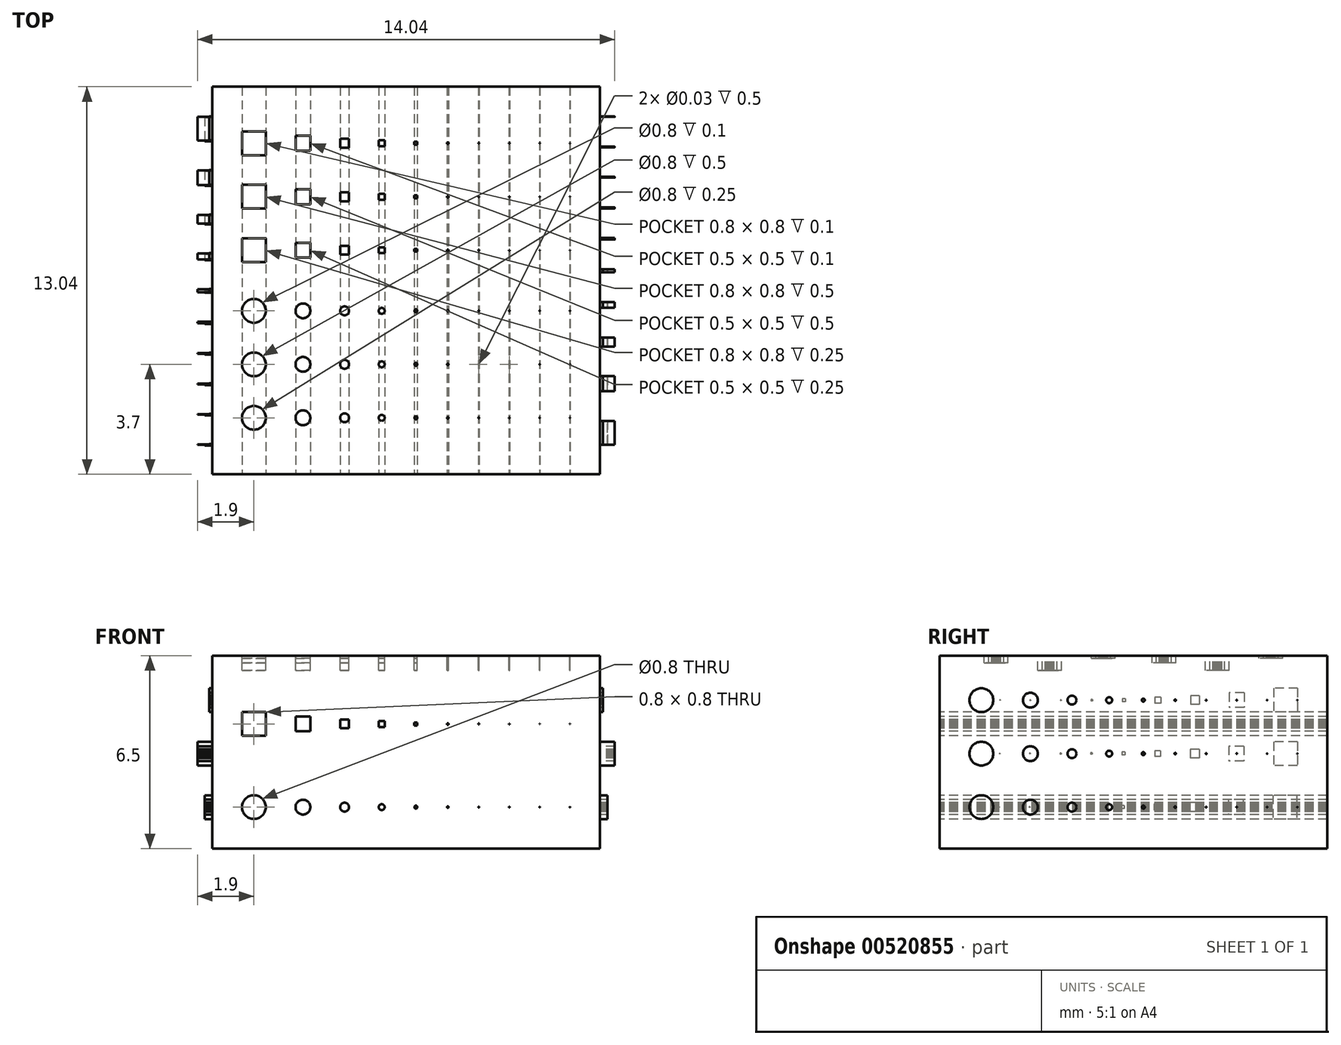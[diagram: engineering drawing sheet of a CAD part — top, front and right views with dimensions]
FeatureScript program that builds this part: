
annotation { "Feature Type Name" : "Feature", "Feature Type Description" : "" }
export const myFeature = defineFeature(function(context is Context, id is Id, definition is map)
    precondition{}
    {
        {
            var Q0;
            Q0=qCreatedBy(makeId("Top.planeOp"),FACE);
            var sketch = newSketch(context, id + "F0", { "sketchPlane" : qUnion([Q0])});
            skLineSegment(sketch, "E0.bottom", {"start": v(-6.52, 6.52) * mm, "end": v(6.52, 6.52) * mm});
            skLineSegment(sketch, "E0.top", {"start": v(-6.52, -6.52) * mm, "end": v(6.52, -6.52) * mm});
            skLineSegment(sketch, "E0.left", {"start": v(-6.52, 6.52) * mm, "end": v(-6.52, -6.52) * mm});
            skLineSegment(sketch, "E0.right", {"start": v(6.52, 6.52) * mm, "end": v(6.52, -6.52) * mm});
            skPoint(sketch, "E0.middle", {"position": v(0, 0) * mm});
            skSolve(sketch);
        }
        {
            var Q0;
            Q0=makeQuery(id+"F0.imprint","IMPRINT",FACE,{"disambiguationData":[TD([[makeQuery(id+"F0.imprint","IMPRINT",EDGE,{"derivedFrom":sQuery(id+"F0.wireOp",EDGE,"E0.bottom")}),-1.0]])]});
            extrude(context, id + "F1", {"entities" : qUnion([Q0]), "depth" : 6.5 * mm, "offsetDistance" : 25 * mm});
        }
        {
            var Q0;
            Q0=makeQuery(id+"F1.opExtrude","SWEPT_FACE",FACE,{"disambiguationData":[OSD([sQuery(id+"F0.wireOp",EDGE,"E0.top")])]});
            var sketch = newSketch(context, id + "F2", { "sketchPlane" : qUnion([Q0])});
            skCircle(sketch, "E1", {"center": v(-5.12, 1.4) * mm, "radius": 0.4 * mm});
            skCircle(sketch, "E2", {"center": v(-3.47, 1.4) * mm, "radius": 0.25 * mm});
            skCircle(sketch, "E3", {"center": v(-2.07, 1.4) * mm, "radius": 0.15 * mm});
            skCircle(sketch, "E4", {"center": v(-0.82, 1.4) * mm, "radius": 0.1 * mm});
            skCircle(sketch, "E5", {"center": v(0.33, 1.4) * mm, "radius": 0.05 * mm});
            skCircle(sketch, "E6", {"center": v(1.4, 1.4) * mm, "radius": 0.03 * mm});
            skCircle(sketch, "E7", {"center": v(2.44, 1.4) * mm, "radius": 0.02 * mm});
            skCircle(sketch, "E8", {"center": v(4.5, 1.4) * mm, "radius": 0 * mm});
            skCircle(sketch, "E9", {"center": v(5.51, 1.4) * mm, "radius": 0 * mm});
            skCircle(sketch, "E10", {"center": v(3.47, 1.4) * mm, "radius": 0.01 * mm});
            skLineSegment(sketch, "E11.bottom", {"start": v(-5.52, 4.6) * mm, "end": v(-4.72, 4.6) * mm});
            skLineSegment(sketch, "E11.top", {"start": v(-5.52, 3.8) * mm, "end": v(-4.72, 3.8) * mm});
            skLineSegment(sketch, "E11.left", {"start": v(-5.52, 4.6) * mm, "end": v(-5.52, 3.8) * mm});
            skLineSegment(sketch, "E11.right", {"start": v(-4.72, 4.6) * mm, "end": v(-4.72, 3.8) * mm});
            skPoint(sketch, "E11.middle", {"position": v(-5.12, 4.2) * mm});
            skLineSegment(sketch, "E12.bottom", {"start": v(-0.92, 4.3) * mm, "end": v(-0.72, 4.3) * mm});
            skLineSegment(sketch, "E12.top", {"start": v(-0.92, 4.1) * mm, "end": v(-0.72, 4.1) * mm});
            skLineSegment(sketch, "E12.left", {"start": v(-0.92, 4.3) * mm, "end": v(-0.92, 4.1) * mm});
            skLineSegment(sketch, "E12.right", {"start": v(-0.72, 4.3) * mm, "end": v(-0.72, 4.1) * mm});
            skPoint(sketch, "E12.middle", {"position": v(-0.82, 4.2) * mm});
            skLineSegment(sketch, "E13.bottom", {"start": v(0.28, 4.25) * mm, "end": v(0.38, 4.25) * mm});
            skLineSegment(sketch, "E13.top", {"start": v(0.28, 4.15) * mm, "end": v(0.38, 4.15) * mm});
            skLineSegment(sketch, "E13.left", {"start": v(0.28, 4.25) * mm, "end": v(0.28, 4.15) * mm});
            skLineSegment(sketch, "E13.right", {"start": v(0.38, 4.25) * mm, "end": v(0.38, 4.15) * mm});
            skPoint(sketch, "E13.middle", {"position": v(0.33, 4.2) * mm});
            skLineSegment(sketch, "E14.bottom", {"start": v(1.38, 4.22) * mm, "end": v(1.43, 4.22) * mm});
            skLineSegment(sketch, "E14.top", {"start": v(1.38, 4.17) * mm, "end": v(1.43, 4.17) * mm});
            skLineSegment(sketch, "E14.left", {"start": v(1.38, 4.22) * mm, "end": v(1.38, 4.17) * mm});
            skLineSegment(sketch, "E14.right", {"start": v(1.43, 4.22) * mm, "end": v(1.43, 4.17) * mm});
            skPoint(sketch, "E14.middle", {"position": v(1.4, 4.2) * mm});
            skLineSegment(sketch, "E15.bottom", {"start": v(2.43, 4.21) * mm, "end": v(2.46, 4.21) * mm});
            skLineSegment(sketch, "E15.top", {"start": v(2.43, 4.18) * mm, "end": v(2.46, 4.18) * mm});
            skLineSegment(sketch, "E15.left", {"start": v(2.43, 4.21) * mm, "end": v(2.43, 4.18) * mm});
            skLineSegment(sketch, "E15.right", {"start": v(2.46, 4.21) * mm, "end": v(2.46, 4.18) * mm});
            skPoint(sketch, "E15.middle", {"position": v(2.45, 4.2) * mm});
            skLineSegment(sketch, "E16.bottom", {"start": v(3.46, 4.21) * mm, "end": v(3.49, 4.21) * mm});
            skLineSegment(sketch, "E16.top", {"start": v(3.46, 4.19) * mm, "end": v(3.49, 4.19) * mm});
            skLineSegment(sketch, "E16.left", {"start": v(3.46, 4.21) * mm, "end": v(3.46, 4.19) * mm});
            skLineSegment(sketch, "E16.right", {"start": v(3.49, 4.21) * mm, "end": v(3.49, 4.19) * mm});
            skPoint(sketch, "E16.middle", {"position": v(3.47, 4.2) * mm});
            skLineSegment(sketch, "E17.bottom", {"start": v(4.49, 4.2) * mm, "end": v(4.5, 4.2) * mm});
            skLineSegment(sketch, "E17.top", {"start": v(4.49, 4.19) * mm, "end": v(4.5, 4.19) * mm});
            skLineSegment(sketch, "E17.left", {"start": v(4.49, 4.2) * mm, "end": v(4.49, 4.19) * mm});
            skLineSegment(sketch, "E17.right", {"start": v(4.5, 4.2) * mm, "end": v(4.5, 4.19) * mm});
            skPoint(sketch, "E17.middle", {"position": v(4.5, 4.2) * mm});
            skLineSegment(sketch, "E18.bottom", {"start": v(5.5, 4.2) * mm, "end": v(5.52, 4.2) * mm});
            skLineSegment(sketch, "E18.top", {"start": v(5.5, 4.2) * mm, "end": v(5.52, 4.2) * mm});
            skLineSegment(sketch, "E18.left", {"start": v(5.5, 4.2) * mm, "end": v(5.5, 4.2) * mm});
            skLineSegment(sketch, "E18.right", {"start": v(5.52, 4.2) * mm, "end": v(5.52, 4.2) * mm});
            skPoint(sketch, "E18.middle", {"position": v(5.51, 4.2) * mm});
            skLineSegment(sketch, "E19.bottom", {"start": v(-3.72, 4.45) * mm, "end": v(-3.22, 4.45) * mm});
            skLineSegment(sketch, "E19.top", {"start": v(-3.72, 3.95) * mm, "end": v(-3.22, 3.95) * mm});
            skLineSegment(sketch, "E19.left", {"start": v(-3.72, 4.45) * mm, "end": v(-3.72, 3.95) * mm});
            skLineSegment(sketch, "E19.right", {"start": v(-3.22, 4.45) * mm, "end": v(-3.22, 3.95) * mm});
            skPoint(sketch, "E19.middle", {"position": v(-3.47, 4.2) * mm});
            skLineSegment(sketch, "E20.bottom", {"start": v(-2.22, 4.35) * mm, "end": v(-1.92, 4.35) * mm});
            skLineSegment(sketch, "E20.top", {"start": v(-2.22, 4.05) * mm, "end": v(-1.92, 4.05) * mm});
            skLineSegment(sketch, "E20.left", {"start": v(-2.22, 4.35) * mm, "end": v(-2.22, 4.05) * mm});
            skLineSegment(sketch, "E20.right", {"start": v(-1.92, 4.35) * mm, "end": v(-1.92, 4.05) * mm});
            skPoint(sketch, "E20.middle", {"position": v(-2.07, 4.2) * mm});
            skSolve(sketch);
        }
        {
            var Q0;
            Q0=makeQuery(id+"F1.opExtrude","SWEPT_FACE",FACE,{"disambiguationData":[OSD([sQuery(id+"F0.wireOp",EDGE,"E0.left")])]});
            var sketch = newSketch(context, id + "F3", { "sketchPlane" : qUnion([Q0])});
            skLineSegment(sketch, "E21.bottom", {"start": v(-5.52, 5.4) * mm, "end": v(-4.72, 5.4) * mm});
            skLineSegment(sketch, "E21.top", {"start": v(-5.52, 4.6) * mm, "end": v(-4.72, 4.6) * mm});
            skLineSegment(sketch, "E21.left", {"start": v(-5.52, 5.4) * mm, "end": v(-5.52, 4.6) * mm});
            skLineSegment(sketch, "E21.right", {"start": v(-4.72, 5.4) * mm, "end": v(-4.72, 4.6) * mm});
            skPoint(sketch, "E21.middle", {"position": v(-5.12, 5) * mm});
            skLineSegment(sketch, "E22.bottom", {"start": v(-0.92, 5.1) * mm, "end": v(-0.72, 5.1) * mm});
            skLineSegment(sketch, "E22.top", {"start": v(-0.92, 4.9) * mm, "end": v(-0.72, 4.9) * mm});
            skLineSegment(sketch, "E22.left", {"start": v(-0.92, 5.1) * mm, "end": v(-0.92, 4.9) * mm});
            skLineSegment(sketch, "E22.right", {"start": v(-0.72, 5.1) * mm, "end": v(-0.72, 4.9) * mm});
            skPoint(sketch, "E22.middle", {"position": v(-0.82, 5) * mm});
            skLineSegment(sketch, "E23.bottom", {"start": v(0.28, 5.05) * mm, "end": v(0.38, 5.05) * mm});
            skLineSegment(sketch, "E23.top", {"start": v(0.28, 4.95) * mm, "end": v(0.38, 4.95) * mm});
            skLineSegment(sketch, "E23.left", {"start": v(0.28, 5.05) * mm, "end": v(0.28, 4.95) * mm});
            skLineSegment(sketch, "E23.right", {"start": v(0.38, 5.05) * mm, "end": v(0.38, 4.95) * mm});
            skPoint(sketch, "E23.middle", {"position": v(0.33, 5) * mm});
            skLineSegment(sketch, "E24.bottom", {"start": v(1.38, 5.03) * mm, "end": v(1.43, 5.03) * mm});
            skLineSegment(sketch, "E24.top", {"start": v(1.38, 4.98) * mm, "end": v(1.43, 4.98) * mm});
            skLineSegment(sketch, "E24.left", {"start": v(1.38, 5.03) * mm, "end": v(1.38, 4.98) * mm});
            skLineSegment(sketch, "E24.right", {"start": v(1.43, 5.03) * mm, "end": v(1.43, 4.98) * mm});
            skPoint(sketch, "E24.middle", {"position": v(1.4, 5) * mm});
            skLineSegment(sketch, "E25.bottom", {"start": v(2.43, 5.02) * mm, "end": v(2.46, 5.02) * mm});
            skLineSegment(sketch, "E25.top", {"start": v(2.43, 4.99) * mm, "end": v(2.46, 4.99) * mm});
            skLineSegment(sketch, "E25.left", {"start": v(2.43, 5.02) * mm, "end": v(2.43, 4.99) * mm});
            skLineSegment(sketch, "E25.right", {"start": v(2.46, 5.02) * mm, "end": v(2.46, 4.99) * mm});
            skPoint(sketch, "E25.middle", {"position": v(2.44, 5) * mm});
            skLineSegment(sketch, "E26.bottom", {"start": v(3.46, 5.01) * mm, "end": v(3.48, 5.01) * mm});
            skLineSegment(sketch, "E26.top", {"start": v(3.46, 4.99) * mm, "end": v(3.48, 4.99) * mm});
            skLineSegment(sketch, "E26.left", {"start": v(3.46, 5.01) * mm, "end": v(3.46, 4.99) * mm});
            skLineSegment(sketch, "E26.right", {"start": v(3.48, 5.01) * mm, "end": v(3.48, 4.99) * mm});
            skPoint(sketch, "E26.middle", {"position": v(3.47, 5) * mm});
            skLineSegment(sketch, "E27.bottom", {"start": v(4.48, 5.01) * mm, "end": v(4.5, 5.01) * mm});
            skLineSegment(sketch, "E27.top", {"start": v(4.48, 5) * mm, "end": v(4.5, 5) * mm});
            skLineSegment(sketch, "E27.left", {"start": v(4.48, 5.01) * mm, "end": v(4.48, 5) * mm});
            skLineSegment(sketch, "E27.right", {"start": v(4.5, 5.01) * mm, "end": v(4.5, 5) * mm});
            skPoint(sketch, "E27.middle", {"position": v(4.5, 5) * mm});
            skLineSegment(sketch, "E28.bottom", {"start": v(5.5, 5) * mm, "end": v(5.52, 5) * mm});
            skLineSegment(sketch, "E28.top", {"start": v(5.5, 5) * mm, "end": v(5.52, 5) * mm});
            skLineSegment(sketch, "E28.left", {"start": v(5.5, 5) * mm, "end": v(5.5, 5) * mm});
            skLineSegment(sketch, "E28.right", {"start": v(5.52, 5) * mm, "end": v(5.52, 5) * mm});
            skPoint(sketch, "E28.middle", {"position": v(5.51, 5) * mm});
            skLineSegment(sketch, "E29.bottom", {"start": v(-3.72, 5.25) * mm, "end": v(-3.22, 5.25) * mm});
            skLineSegment(sketch, "E29.top", {"start": v(-3.72, 4.75) * mm, "end": v(-3.22, 4.75) * mm});
            skLineSegment(sketch, "E29.left", {"start": v(-3.72, 5.25) * mm, "end": v(-3.72, 4.75) * mm});
            skLineSegment(sketch, "E29.right", {"start": v(-3.22, 5.25) * mm, "end": v(-3.22, 4.75) * mm});
            skPoint(sketch, "E29.middle", {"position": v(-3.47, 5) * mm});
            skLineSegment(sketch, "E30.bottom", {"start": v(-2.22, 5.15) * mm, "end": v(-1.92, 5.15) * mm});
            skLineSegment(sketch, "E30.top", {"start": v(-2.22, 4.85) * mm, "end": v(-1.92, 4.85) * mm});
            skLineSegment(sketch, "E30.left", {"start": v(-2.22, 5.15) * mm, "end": v(-2.22, 4.85) * mm});
            skLineSegment(sketch, "E30.right", {"start": v(-1.92, 5.15) * mm, "end": v(-1.92, 4.85) * mm});
            skPoint(sketch, "E30.middle", {"position": v(-2.07, 5) * mm});
            skLineSegment(sketch, "E31.bottom", {"start": v(-5.51, 3.6) * mm, "end": v(-4.71, 3.6) * mm});
            skLineSegment(sketch, "E31.top", {"start": v(-5.51, 2.8) * mm, "end": v(-4.71, 2.8) * mm});
            skLineSegment(sketch, "E31.left", {"start": v(-5.51, 3.6) * mm, "end": v(-5.51, 2.8) * mm});
            skLineSegment(sketch, "E31.right", {"start": v(-4.71, 3.6) * mm, "end": v(-4.71, 2.8) * mm});
            skPoint(sketch, "E31.middle", {"position": v(-5.11, 3.2) * mm});
            skLineSegment(sketch, "E32.bottom", {"start": v(-0.91, 3.3) * mm, "end": v(-0.71, 3.3) * mm});
            skLineSegment(sketch, "E32.top", {"start": v(-0.91, 3.1) * mm, "end": v(-0.71, 3.1) * mm});
            skLineSegment(sketch, "E32.left", {"start": v(-0.91, 3.3) * mm, "end": v(-0.91, 3.1) * mm});
            skLineSegment(sketch, "E32.right", {"start": v(-0.71, 3.3) * mm, "end": v(-0.71, 3.1) * mm});
            skPoint(sketch, "E32.middle", {"position": v(-0.81, 3.2) * mm});
            skLineSegment(sketch, "E33.bottom", {"start": v(0.29, 3.25) * mm, "end": v(0.39, 3.25) * mm});
            skLineSegment(sketch, "E33.top", {"start": v(0.29, 3.15) * mm, "end": v(0.39, 3.15) * mm});
            skLineSegment(sketch, "E33.left", {"start": v(0.29, 3.25) * mm, "end": v(0.29, 3.15) * mm});
            skLineSegment(sketch, "E33.right", {"start": v(0.39, 3.25) * mm, "end": v(0.39, 3.15) * mm});
            skPoint(sketch, "E33.middle", {"position": v(0.34, 3.2) * mm});
            skLineSegment(sketch, "E34.bottom", {"start": v(1.39, 3.23) * mm, "end": v(1.44, 3.23) * mm});
            skLineSegment(sketch, "E34.top", {"start": v(1.39, 3.18) * mm, "end": v(1.44, 3.18) * mm});
            skLineSegment(sketch, "E34.left", {"start": v(1.39, 3.23) * mm, "end": v(1.39, 3.18) * mm});
            skLineSegment(sketch, "E34.right", {"start": v(1.44, 3.23) * mm, "end": v(1.44, 3.18) * mm});
            skPoint(sketch, "E34.middle", {"position": v(1.41, 3.2) * mm});
            skLineSegment(sketch, "E35.bottom", {"start": v(2.44, 3.22) * mm, "end": v(2.47, 3.22) * mm});
            skLineSegment(sketch, "E35.top", {"start": v(2.44, 3.19) * mm, "end": v(2.47, 3.19) * mm});
            skLineSegment(sketch, "E35.left", {"start": v(2.44, 3.22) * mm, "end": v(2.44, 3.19) * mm});
            skLineSegment(sketch, "E35.right", {"start": v(2.47, 3.22) * mm, "end": v(2.47, 3.19) * mm});
            skPoint(sketch, "E35.middle", {"position": v(2.45, 3.2) * mm});
            skLineSegment(sketch, "E36.bottom", {"start": v(3.47, 3.21) * mm, "end": v(3.5, 3.21) * mm});
            skLineSegment(sketch, "E36.top", {"start": v(3.47, 3.19) * mm, "end": v(3.5, 3.19) * mm});
            skLineSegment(sketch, "E36.left", {"start": v(3.47, 3.21) * mm, "end": v(3.47, 3.19) * mm});
            skLineSegment(sketch, "E36.right", {"start": v(3.5, 3.21) * mm, "end": v(3.5, 3.19) * mm});
            skPoint(sketch, "E36.middle", {"position": v(3.48, 3.2) * mm});
            skLineSegment(sketch, "E37.bottom", {"start": v(4.5, 3.2) * mm, "end": v(4.51, 3.2) * mm});
            skLineSegment(sketch, "E37.top", {"start": v(4.5, 3.19) * mm, "end": v(4.51, 3.19) * mm});
            skLineSegment(sketch, "E37.left", {"start": v(4.5, 3.21) * mm, "end": v(4.5, 3.2) * mm});
            skLineSegment(sketch, "E37.right", {"start": v(4.51, 3.2) * mm, "end": v(4.51, 3.2) * mm});
            skPoint(sketch, "E37.middle", {"position": v(4.5, 3.2) * mm});
            skLineSegment(sketch, "E38.bottom", {"start": v(5.51, 3.2) * mm, "end": v(5.53, 3.2) * mm});
            skLineSegment(sketch, "E38.top", {"start": v(5.51, 3.2) * mm, "end": v(5.53, 3.2) * mm});
            skLineSegment(sketch, "E38.left", {"start": v(5.51, 3.2) * mm, "end": v(5.51, 3.2) * mm});
            skLineSegment(sketch, "E38.right", {"start": v(5.53, 3.2) * mm, "end": v(5.53, 3.2) * mm});
            skPoint(sketch, "E38.middle", {"position": v(5.52, 3.2) * mm});
            skLineSegment(sketch, "E39.bottom", {"start": v(-3.71, 3.45) * mm, "end": v(-3.21, 3.45) * mm});
            skLineSegment(sketch, "E39.top", {"start": v(-3.71, 2.95) * mm, "end": v(-3.21, 2.95) * mm});
            skLineSegment(sketch, "E39.left", {"start": v(-3.71, 3.45) * mm, "end": v(-3.71, 2.95) * mm});
            skLineSegment(sketch, "E39.right", {"start": v(-3.21, 3.45) * mm, "end": v(-3.21, 2.95) * mm});
            skPoint(sketch, "E39.middle", {"position": v(-3.46, 3.2) * mm});
            skLineSegment(sketch, "E40.bottom", {"start": v(-2.21, 3.35) * mm, "end": v(-1.91, 3.35) * mm});
            skLineSegment(sketch, "E40.top", {"start": v(-2.21, 3.05) * mm, "end": v(-1.91, 3.05) * mm});
            skLineSegment(sketch, "E40.left", {"start": v(-2.21, 3.35) * mm, "end": v(-2.21, 3.05) * mm});
            skLineSegment(sketch, "E40.right", {"start": v(-1.91, 3.35) * mm, "end": v(-1.91, 3.05) * mm});
            skPoint(sketch, "E40.middle", {"position": v(-2.06, 3.2) * mm});
            skLineSegment(sketch, "E41.bottom", {"start": v(-5.49, 1.8) * mm, "end": v(-4.69, 1.8) * mm});
            skLineSegment(sketch, "E41.top", {"start": v(-5.49, 1) * mm, "end": v(-4.69, 1) * mm});
            skLineSegment(sketch, "E41.left", {"start": v(-5.49, 1.8) * mm, "end": v(-5.49, 1) * mm});
            skLineSegment(sketch, "E41.right", {"start": v(-4.69, 1.8) * mm, "end": v(-4.69, 1) * mm});
            skPoint(sketch, "E41.middle", {"position": v(-5.09, 1.4) * mm});
            skLineSegment(sketch, "E42.bottom", {"start": v(-0.89, 1.5) * mm, "end": v(-0.69, 1.5) * mm});
            skLineSegment(sketch, "E42.top", {"start": v(-0.89, 1.3) * mm, "end": v(-0.69, 1.3) * mm});
            skLineSegment(sketch, "E42.left", {"start": v(-0.89, 1.5) * mm, "end": v(-0.89, 1.3) * mm});
            skLineSegment(sketch, "E42.right", {"start": v(-0.69, 1.5) * mm, "end": v(-0.69, 1.3) * mm});
            skPoint(sketch, "E42.middle", {"position": v(-0.79, 1.4) * mm});
            skLineSegment(sketch, "E43.bottom", {"start": v(0.31, 1.45) * mm, "end": v(0.41, 1.45) * mm});
            skLineSegment(sketch, "E43.top", {"start": v(0.31, 1.35) * mm, "end": v(0.41, 1.35) * mm});
            skLineSegment(sketch, "E43.left", {"start": v(0.31, 1.45) * mm, "end": v(0.31, 1.35) * mm});
            skLineSegment(sketch, "E43.right", {"start": v(0.41, 1.45) * mm, "end": v(0.41, 1.35) * mm});
            skPoint(sketch, "E43.middle", {"position": v(0.36, 1.4) * mm});
            skLineSegment(sketch, "E44.bottom", {"start": v(1.41, 1.42) * mm, "end": v(1.46, 1.42) * mm});
            skLineSegment(sketch, "E44.top", {"start": v(1.41, 1.37) * mm, "end": v(1.46, 1.37) * mm});
            skLineSegment(sketch, "E44.left", {"start": v(1.41, 1.42) * mm, "end": v(1.41, 1.37) * mm});
            skLineSegment(sketch, "E44.right", {"start": v(1.46, 1.42) * mm, "end": v(1.46, 1.37) * mm});
            skPoint(sketch, "E44.middle", {"position": v(1.44, 1.4) * mm});
            skLineSegment(sketch, "E45.bottom", {"start": v(2.46, 1.41) * mm, "end": v(2.5, 1.41) * mm});
            skLineSegment(sketch, "E45.top", {"start": v(2.46, 1.38) * mm, "end": v(2.5, 1.38) * mm});
            skLineSegment(sketch, "E45.left", {"start": v(2.46, 1.41) * mm, "end": v(2.46, 1.38) * mm});
            skLineSegment(sketch, "E45.right", {"start": v(2.5, 1.41) * mm, "end": v(2.5, 1.38) * mm});
            skPoint(sketch, "E45.middle", {"position": v(2.48, 1.4) * mm});
            skLineSegment(sketch, "E46.bottom", {"start": v(3.5, 1.41) * mm, "end": v(3.52, 1.41) * mm});
            skLineSegment(sketch, "E46.top", {"start": v(3.5, 1.39) * mm, "end": v(3.52, 1.39) * mm});
            skLineSegment(sketch, "E46.left", {"start": v(3.5, 1.41) * mm, "end": v(3.5, 1.39) * mm});
            skLineSegment(sketch, "E46.right", {"start": v(3.52, 1.41) * mm, "end": v(3.52, 1.39) * mm});
            skPoint(sketch, "E46.middle", {"position": v(3.5, 1.4) * mm});
            skLineSegment(sketch, "E47.bottom", {"start": v(4.52, 1.4) * mm, "end": v(4.54, 1.4) * mm});
            skLineSegment(sketch, "E47.top", {"start": v(4.52, 1.39) * mm, "end": v(4.54, 1.39) * mm});
            skLineSegment(sketch, "E47.left", {"start": v(4.52, 1.4) * mm, "end": v(4.52, 1.39) * mm});
            skLineSegment(sketch, "E47.right", {"start": v(4.54, 1.4) * mm, "end": v(4.54, 1.39) * mm});
            skPoint(sketch, "E47.middle", {"position": v(4.53, 1.4) * mm});
            skLineSegment(sketch, "E48.bottom", {"start": v(5.54, 1.4) * mm, "end": v(5.55, 1.4) * mm});
            skLineSegment(sketch, "E48.top", {"start": v(5.54, 1.4) * mm, "end": v(5.55, 1.4) * mm});
            skLineSegment(sketch, "E48.left", {"start": v(5.54, 1.4) * mm, "end": v(5.54, 1.4) * mm});
            skLineSegment(sketch, "E48.right", {"start": v(5.55, 1.4) * mm, "end": v(5.55, 1.4) * mm});
            skPoint(sketch, "E48.middle", {"position": v(5.55, 1.4) * mm});
            skLineSegment(sketch, "E49.bottom", {"start": v(-3.69, 1.65) * mm, "end": v(-3.19, 1.65) * mm});
            skLineSegment(sketch, "E49.top", {"start": v(-3.69, 1.15) * mm, "end": v(-3.19, 1.15) * mm});
            skLineSegment(sketch, "E49.left", {"start": v(-3.69, 1.65) * mm, "end": v(-3.69, 1.15) * mm});
            skLineSegment(sketch, "E49.right", {"start": v(-3.19, 1.65) * mm, "end": v(-3.19, 1.15) * mm});
            skPoint(sketch, "E49.middle", {"position": v(-3.44, 1.4) * mm});
            skLineSegment(sketch, "E50.bottom", {"start": v(-2.19, 1.55) * mm, "end": v(-1.89, 1.55) * mm});
            skLineSegment(sketch, "E50.top", {"start": v(-2.19, 1.25) * mm, "end": v(-1.89, 1.25) * mm});
            skLineSegment(sketch, "E50.left", {"start": v(-2.19, 1.55) * mm, "end": v(-2.19, 1.25) * mm});
            skLineSegment(sketch, "E50.right", {"start": v(-1.89, 1.55) * mm, "end": v(-1.89, 1.25) * mm});
            skPoint(sketch, "E50.middle", {"position": v(-2.04, 1.4) * mm});
            skSolve(sketch);
        }
        {
            var Q0;
            Q0=makeQuery(id+"F1.opExtrude","SWEPT_FACE",FACE,{"disambiguationData":[OSD([sQuery(id+"F0.wireOp",EDGE,"E0.right")])]});
            var sketch = newSketch(context, id + "F4", { "sketchPlane" : qUnion([Q0])});
            skCircle(sketch, "E51", {"center": v(-5.12, 1.4) * mm, "radius": 0.4 * mm});
            skCircle(sketch, "E52", {"center": v(-3.47, 1.4) * mm, "radius": 0.25 * mm});
            skCircle(sketch, "E53", {"center": v(-2.07, 1.4) * mm, "radius": 0.15 * mm});
            skCircle(sketch, "E54", {"center": v(-0.82, 1.4) * mm, "radius": 0.1 * mm});
            skCircle(sketch, "E55", {"center": v(0.33, 1.4) * mm, "radius": 0.05 * mm});
            skCircle(sketch, "E56", {"center": v(1.4, 1.4) * mm, "radius": 0.03 * mm});
            skCircle(sketch, "E57", {"center": v(2.44, 1.4) * mm, "radius": 0.02 * mm});
            skCircle(sketch, "E58", {"center": v(4.5, 1.4) * mm, "radius": 0 * mm});
            skCircle(sketch, "E59", {"center": v(5.51, 1.4) * mm, "radius": 0 * mm});
            skCircle(sketch, "E60", {"center": v(3.47, 1.4) * mm, "radius": 0.01 * mm});
            skCircle(sketch, "E61", {"center": v(-5.12, 3.2) * mm, "radius": 0.4 * mm});
            skCircle(sketch, "E62", {"center": v(-3.47, 3.2) * mm, "radius": 0.25 * mm});
            skCircle(sketch, "E63", {"center": v(-2.07, 3.2) * mm, "radius": 0.15 * mm});
            skCircle(sketch, "E64", {"center": v(-0.82, 3.2) * mm, "radius": 0.1 * mm});
            skCircle(sketch, "E65", {"center": v(0.33, 3.2) * mm, "radius": 0.05 * mm});
            skCircle(sketch, "E66", {"center": v(1.4, 3.2) * mm, "radius": 0.03 * mm});
            skCircle(sketch, "E67", {"center": v(2.44, 3.2) * mm, "radius": 0.02 * mm});
            skCircle(sketch, "E68", {"center": v(4.5, 3.2) * mm, "radius": 0 * mm});
            skCircle(sketch, "E69", {"center": v(5.51, 3.2) * mm, "radius": 0 * mm});
            skCircle(sketch, "E70", {"center": v(3.47, 3.2) * mm, "radius": 0.01 * mm});
            skCircle(sketch, "E71", {"center": v(-5.12, 5) * mm, "radius": 0.4 * mm});
            skCircle(sketch, "E72", {"center": v(-3.47, 5) * mm, "radius": 0.25 * mm});
            skCircle(sketch, "E73", {"center": v(-2.07, 5) * mm, "radius": 0.15 * mm});
            skCircle(sketch, "E74", {"center": v(-0.82, 5) * mm, "radius": 0.1 * mm});
            skCircle(sketch, "E75", {"center": v(0.33, 5) * mm, "radius": 0.05 * mm});
            skCircle(sketch, "E76", {"center": v(1.4, 5) * mm, "radius": 0.03 * mm});
            skCircle(sketch, "E77", {"center": v(2.44, 5) * mm, "radius": 0.02 * mm});
            skCircle(sketch, "E78", {"center": v(4.5, 5) * mm, "radius": 0 * mm});
            skCircle(sketch, "E79", {"center": v(5.51, 5) * mm, "radius": 0 * mm});
            skCircle(sketch, "E80", {"center": v(3.47, 5) * mm, "radius": 0.01 * mm});
            skSolve(sketch);
        }
        {
            var Q0;
            Q0=makeQuery(id+"F2.imprint","IMPRINT",FACE,{"disambiguationData":[TD([[makeQuery(id+"F2.imprint","IMPRINT",EDGE,{"derivedFrom":sQuery(id+"F2.wireOp",EDGE,"E1")}),1.0]])]});
            var Q1;
            Q1=makeQuery(id+"F2.imprint","IMPRINT",FACE,{"disambiguationData":[TD([[makeQuery(id+"F2.imprint","IMPRINT",EDGE,{"derivedFrom":sQuery(id+"F2.wireOp",EDGE,"E2")}),1.0]])]});
            var Q2;
            Q2=makeQuery(id+"F2.imprint","IMPRINT",FACE,{"disambiguationData":[TD([[makeQuery(id+"F2.imprint","IMPRINT",EDGE,{"derivedFrom":sQuery(id+"F2.wireOp",EDGE,"E3")}),1.0]])]});
            var Q3;
            Q3=makeQuery(id+"F2.imprint","IMPRINT",FACE,{"disambiguationData":[TD([[makeQuery(id+"F2.imprint","IMPRINT",EDGE,{"derivedFrom":sQuery(id+"F2.wireOp",EDGE,"E9")}),1.0]])]});
            var Q4;
            Q4=makeQuery(id+"F2.imprint","IMPRINT",FACE,{"disambiguationData":[TD([[makeQuery(id+"F2.imprint","IMPRINT",EDGE,{"derivedFrom":sQuery(id+"F2.wireOp",EDGE,"E8")}),1.0]])]});
            var Q5;
            Q5=makeQuery(id+"F2.imprint","IMPRINT",FACE,{"disambiguationData":[TD([[makeQuery(id+"F2.imprint","IMPRINT",EDGE,{"derivedFrom":sQuery(id+"F2.wireOp",EDGE,"E10")}),1.0]])]});
            var Q6;
            Q6=makeQuery(id+"F2.imprint","IMPRINT",FACE,{"disambiguationData":[TD([[makeQuery(id+"F2.imprint","IMPRINT",EDGE,{"derivedFrom":sQuery(id+"F2.wireOp",EDGE,"E7")}),1.0]])]});
            var Q7;
            Q7=makeQuery(id+"F2.imprint","IMPRINT",FACE,{"disambiguationData":[TD([[makeQuery(id+"F2.imprint","IMPRINT",EDGE,{"derivedFrom":sQuery(id+"F2.wireOp",EDGE,"E6")}),1.0]])]});
            var Q8;
            Q8=makeQuery(id+"F2.imprint","IMPRINT",FACE,{"disambiguationData":[TD([[makeQuery(id+"F2.imprint","IMPRINT",EDGE,{"derivedFrom":sQuery(id+"F2.wireOp",EDGE,"E5")}),1.0]])]});
            var Q9;
            Q9=makeQuery(id+"F2.imprint","IMPRINT",FACE,{"disambiguationData":[TD([[makeQuery(id+"F2.imprint","IMPRINT",EDGE,{"derivedFrom":sQuery(id+"F2.wireOp",EDGE,"E4")}),1.0]])]});
            var Q10;
            Q10=makeQuery(id+"F2.imprint","IMPRINT",FACE,{"disambiguationData":[TD([[makeQuery(id+"F2.imprint","IMPRINT",EDGE,{"derivedFrom":sQuery(id+"F2.wireOp",EDGE,"E11.bottom")}),-1.0]])]});
            var Q11;
            Q11=makeQuery(id+"F2.imprint","IMPRINT",FACE,{"disambiguationData":[TD([[makeQuery(id+"F2.imprint","IMPRINT",EDGE,{"derivedFrom":sQuery(id+"F2.wireOp",EDGE,"E19.bottom")}),-1.0]])]});
            var Q12;
            Q12=makeQuery(id+"F2.imprint","IMPRINT",FACE,{"disambiguationData":[TD([[makeQuery(id+"F2.imprint","IMPRINT",EDGE,{"derivedFrom":sQuery(id+"F2.wireOp",EDGE,"E20.bottom")}),-1.0]])]});
            var Q13;
            Q13=makeQuery(id+"F2.imprint","IMPRINT",FACE,{"disambiguationData":[TD([[makeQuery(id+"F2.imprint","IMPRINT",EDGE,{"derivedFrom":sQuery(id+"F2.wireOp",EDGE,"E12.bottom")}),-1.0]])]});
            var Q14;
            Q14=makeQuery(id+"F2.imprint","IMPRINT",FACE,{"disambiguationData":[TD([[makeQuery(id+"F2.imprint","IMPRINT",EDGE,{"derivedFrom":sQuery(id+"F2.wireOp",EDGE,"E13.bottom")}),-1.0]])]});
            var Q15;
            Q15=makeQuery(id+"F2.imprint","IMPRINT",FACE,{"disambiguationData":[TD([[makeQuery(id+"F2.imprint","IMPRINT",EDGE,{"derivedFrom":sQuery(id+"F2.wireOp",EDGE,"E14.bottom")}),-1.0]])]});
            var Q16;
            Q16=makeQuery(id+"F2.imprint","IMPRINT",FACE,{"disambiguationData":[TD([[makeQuery(id+"F2.imprint","IMPRINT",EDGE,{"derivedFrom":sQuery(id+"F2.wireOp",EDGE,"E15.bottom")}),-1.0]])]});
            var Q17;
            Q17=makeQuery(id+"F2.imprint","IMPRINT",FACE,{"disambiguationData":[TD([[makeQuery(id+"F2.imprint","IMPRINT",EDGE,{"derivedFrom":sQuery(id+"F2.wireOp",EDGE,"E16.bottom")}),-1.0]])]});
            var Q18;
            Q18=makeQuery(id+"F2.imprint","IMPRINT",FACE,{"disambiguationData":[TD([[makeQuery(id+"F2.imprint","IMPRINT",EDGE,{"derivedFrom":sQuery(id+"F2.wireOp",EDGE,"E17.bottom")}),-1.0]])]});
            var Q19;
            Q19=makeQuery(id+"F2.imprint","IMPRINT",FACE,{"disambiguationData":[TD([[makeQuery(id+"F2.imprint","IMPRINT",EDGE,{"derivedFrom":sQuery(id+"F2.wireOp",EDGE,"E18.bottom")}),-1.0]])]});
            extrude(context, id + "F5", {"entities" : qUnion([Q0, Q1, Q2, Q3, Q4, Q5, Q6, Q7, Q8, Q9, Q10, Q11, Q12, Q13, Q14, Q15, Q16, Q17, Q18, Q19]), "operationType" : NewBodyOperationType.REMOVE, "oppositeDirection" : true, "depth" : 25 * mm, "offsetDistance" : 25 * mm});
        }
        {
            var Q0;
            Q0=makeQuery(id+"F1.opExtrude","CAP_FACE",FACE,{"disambiguationData":[OSD([sQuery(id+"F0.wireOp",EDGE,"E0.bottom"),sQuery(id+"F0.wireOp",EDGE,"E0.top"),sQuery(id+"F0.wireOp",EDGE,"E0.left"),sQuery(id+"F0.wireOp",EDGE,"E0.right")])],"isStart":false});
            var sketch = newSketch(context, id + "F6", { "sketchPlane" : qUnion([Q0])});
            skCircle(sketch, "E81", {"center": v(-5.12, -4.62) * mm, "radius": 0.4 * mm});
            skCircle(sketch, "E82", {"center": v(-3.47, -4.62) * mm, "radius": 0.25 * mm});
            skCircle(sketch, "E83", {"center": v(-2.07, -4.62) * mm, "radius": 0.15 * mm});
            skCircle(sketch, "E84", {"center": v(-0.82, -4.62) * mm, "radius": 0.1 * mm});
            skCircle(sketch, "E85", {"center": v(0.33, -4.62) * mm, "radius": 0.05 * mm});
            skCircle(sketch, "E86", {"center": v(1.4, -4.62) * mm, "radius": 0.03 * mm});
            skCircle(sketch, "E87", {"center": v(2.44, -4.62) * mm, "radius": 0.02 * mm});
            skCircle(sketch, "E88", {"center": v(4.5, -4.62) * mm, "radius": 0 * mm});
            skCircle(sketch, "E89", {"center": v(5.51, -4.62) * mm, "radius": 0 * mm});
            skCircle(sketch, "E90", {"center": v(3.47, -4.62) * mm, "radius": 0.01 * mm});
            skCircle(sketch, "E91", {"center": v(-5.12, -2.82) * mm, "radius": 0.4 * mm});
            skCircle(sketch, "E92", {"center": v(-3.47, -2.82) * mm, "radius": 0.25 * mm});
            skCircle(sketch, "E93", {"center": v(-2.07, -2.82) * mm, "radius": 0.15 * mm});
            skCircle(sketch, "E94", {"center": v(-0.82, -2.82) * mm, "radius": 0.1 * mm});
            skCircle(sketch, "E95", {"center": v(0.33, -2.82) * mm, "radius": 0.05 * mm});
            skCircle(sketch, "E96", {"center": v(1.4, -2.82) * mm, "radius": 0.03 * mm});
            skCircle(sketch, "E97", {"center": v(2.44, -2.82) * mm, "radius": 0.02 * mm});
            skCircle(sketch, "E98", {"center": v(4.5, -2.82) * mm, "radius": 0 * mm});
            skCircle(sketch, "E99", {"center": v(5.51, -2.82) * mm, "radius": 0 * mm});
            skCircle(sketch, "E100", {"center": v(3.47, -2.82) * mm, "radius": 0.01 * mm});
            skCircle(sketch, "E101", {"center": v(-5.12, -1.02) * mm, "radius": 0.4 * mm});
            skCircle(sketch, "E102", {"center": v(-3.47, -1.02) * mm, "radius": 0.25 * mm});
            skCircle(sketch, "E103", {"center": v(-2.07, -1.02) * mm, "radius": 0.15 * mm});
            skCircle(sketch, "E104", {"center": v(-0.82, -1.02) * mm, "radius": 0.1 * mm});
            skCircle(sketch, "E105", {"center": v(0.33, -1.02) * mm, "radius": 0.05 * mm});
            skCircle(sketch, "E106", {"center": v(1.4, -1.02) * mm, "radius": 0.03 * mm});
            skCircle(sketch, "E107", {"center": v(2.44, -1.02) * mm, "radius": 0.02 * mm});
            skCircle(sketch, "E108", {"center": v(4.5, -1.02) * mm, "radius": 0 * mm});
            skCircle(sketch, "E109", {"center": v(5.51, -1.02) * mm, "radius": 0 * mm});
            skCircle(sketch, "E110", {"center": v(3.47, -1.02) * mm, "radius": 0.01 * mm});
            skLineSegment(sketch, "E111.bottom", {"start": v(-5.52, 5.02) * mm, "end": v(-4.72, 5.02) * mm});
            skLineSegment(sketch, "E111.top", {"start": v(-5.52, 4.22) * mm, "end": v(-4.72, 4.22) * mm});
            skLineSegment(sketch, "E111.left", {"start": v(-5.52, 5.02) * mm, "end": v(-5.52, 4.22) * mm});
            skLineSegment(sketch, "E111.right", {"start": v(-4.72, 5.02) * mm, "end": v(-4.72, 4.22) * mm});
            skPoint(sketch, "E111.middle", {"position": v(-5.12, 4.62) * mm});
            skLineSegment(sketch, "E112.bottom", {"start": v(-0.92, 4.72) * mm, "end": v(-0.72, 4.72) * mm});
            skLineSegment(sketch, "E112.top", {"start": v(-0.92, 4.52) * mm, "end": v(-0.72, 4.52) * mm});
            skLineSegment(sketch, "E112.left", {"start": v(-0.92, 4.72) * mm, "end": v(-0.92, 4.52) * mm});
            skLineSegment(sketch, "E112.right", {"start": v(-0.72, 4.72) * mm, "end": v(-0.72, 4.52) * mm});
            skPoint(sketch, "E112.middle", {"position": v(-0.82, 4.62) * mm});
            skLineSegment(sketch, "E113.bottom", {"start": v(0.28, 4.67) * mm, "end": v(0.38, 4.67) * mm});
            skLineSegment(sketch, "E113.top", {"start": v(0.28, 4.57) * mm, "end": v(0.38, 4.57) * mm});
            skLineSegment(sketch, "E113.left", {"start": v(0.28, 4.67) * mm, "end": v(0.28, 4.57) * mm});
            skLineSegment(sketch, "E113.right", {"start": v(0.38, 4.67) * mm, "end": v(0.38, 4.57) * mm});
            skPoint(sketch, "E113.middle", {"position": v(0.33, 4.62) * mm});
            skLineSegment(sketch, "E114.bottom", {"start": v(1.38, 4.65) * mm, "end": v(1.43, 4.65) * mm});
            skLineSegment(sketch, "E114.top", {"start": v(1.38, 4.6) * mm, "end": v(1.43, 4.6) * mm});
            skLineSegment(sketch, "E114.left", {"start": v(1.38, 4.65) * mm, "end": v(1.38, 4.6) * mm});
            skLineSegment(sketch, "E114.right", {"start": v(1.43, 4.65) * mm, "end": v(1.43, 4.6) * mm});
            skPoint(sketch, "E114.middle", {"position": v(1.4, 4.62) * mm});
            skLineSegment(sketch, "E115.bottom", {"start": v(2.43, 4.64) * mm, "end": v(2.46, 4.64) * mm});
            skLineSegment(sketch, "E115.top", {"start": v(2.43, 4.6) * mm, "end": v(2.46, 4.6) * mm});
            skLineSegment(sketch, "E115.left", {"start": v(2.43, 4.64) * mm, "end": v(2.43, 4.6) * mm});
            skLineSegment(sketch, "E115.right", {"start": v(2.46, 4.64) * mm, "end": v(2.46, 4.6) * mm});
            skPoint(sketch, "E115.middle", {"position": v(2.44, 4.62) * mm});
            skLineSegment(sketch, "E116.bottom", {"start": v(3.46, 4.63) * mm, "end": v(3.48, 4.63) * mm});
            skLineSegment(sketch, "E116.top", {"start": v(3.46, 4.6) * mm, "end": v(3.48, 4.6) * mm});
            skLineSegment(sketch, "E116.left", {"start": v(3.46, 4.63) * mm, "end": v(3.46, 4.6) * mm});
            skLineSegment(sketch, "E116.right", {"start": v(3.48, 4.63) * mm, "end": v(3.48, 4.6) * mm});
            skPoint(sketch, "E116.middle", {"position": v(3.47, 4.62) * mm});
            skLineSegment(sketch, "E117.bottom", {"start": v(4.48, 4.63) * mm, "end": v(4.5, 4.63) * mm});
            skLineSegment(sketch, "E117.top", {"start": v(4.48, 4.61) * mm, "end": v(4.5, 4.61) * mm});
            skLineSegment(sketch, "E117.left", {"start": v(4.48, 4.63) * mm, "end": v(4.48, 4.61) * mm});
            skLineSegment(sketch, "E117.right", {"start": v(4.5, 4.63) * mm, "end": v(4.5, 4.61) * mm});
            skPoint(sketch, "E117.middle", {"position": v(4.5, 4.62) * mm});
            skLineSegment(sketch, "E118.bottom", {"start": v(5.5, 4.63) * mm, "end": v(5.52, 4.63) * mm});
            skLineSegment(sketch, "E118.top", {"start": v(5.5, 4.61) * mm, "end": v(5.52, 4.61) * mm});
            skLineSegment(sketch, "E118.left", {"start": v(5.5, 4.63) * mm, "end": v(5.5, 4.61) * mm});
            skLineSegment(sketch, "E118.right", {"start": v(5.52, 4.63) * mm, "end": v(5.52, 4.61) * mm});
            skPoint(sketch, "E118.middle", {"position": v(5.51, 4.62) * mm});
            skLineSegment(sketch, "E119.bottom", {"start": v(-3.72, 4.87) * mm, "end": v(-3.22, 4.87) * mm});
            skLineSegment(sketch, "E119.top", {"start": v(-3.72, 4.37) * mm, "end": v(-3.22, 4.37) * mm});
            skLineSegment(sketch, "E119.left", {"start": v(-3.72, 4.87) * mm, "end": v(-3.72, 4.37) * mm});
            skLineSegment(sketch, "E119.right", {"start": v(-3.22, 4.87) * mm, "end": v(-3.22, 4.37) * mm});
            skPoint(sketch, "E119.middle", {"position": v(-3.47, 4.62) * mm});
            skLineSegment(sketch, "E120.bottom", {"start": v(-2.22, 4.77) * mm, "end": v(-1.92, 4.77) * mm});
            skLineSegment(sketch, "E120.top", {"start": v(-2.22, 4.47) * mm, "end": v(-1.92, 4.47) * mm});
            skLineSegment(sketch, "E120.left", {"start": v(-2.22, 4.77) * mm, "end": v(-2.22, 4.47) * mm});
            skLineSegment(sketch, "E120.right", {"start": v(-1.92, 4.77) * mm, "end": v(-1.92, 4.47) * mm});
            skPoint(sketch, "E120.middle", {"position": v(-2.07, 4.62) * mm});
            skLineSegment(sketch, "E121.bottom", {"start": v(-5.52, 3.22) * mm, "end": v(-4.72, 3.22) * mm});
            skLineSegment(sketch, "E121.top", {"start": v(-5.52, 2.42) * mm, "end": v(-4.72, 2.42) * mm});
            skLineSegment(sketch, "E121.left", {"start": v(-5.52, 3.22) * mm, "end": v(-5.52, 2.42) * mm});
            skLineSegment(sketch, "E121.right", {"start": v(-4.72, 3.22) * mm, "end": v(-4.72, 2.42) * mm});
            skPoint(sketch, "E121.middle", {"position": v(-5.12, 2.82) * mm});
            skLineSegment(sketch, "E122.bottom", {"start": v(-0.92, 2.92) * mm, "end": v(-0.72, 2.92) * mm});
            skLineSegment(sketch, "E122.top", {"start": v(-0.92, 2.72) * mm, "end": v(-0.72, 2.72) * mm});
            skLineSegment(sketch, "E122.left", {"start": v(-0.92, 2.92) * mm, "end": v(-0.92, 2.72) * mm});
            skLineSegment(sketch, "E122.right", {"start": v(-0.72, 2.92) * mm, "end": v(-0.72, 2.72) * mm});
            skPoint(sketch, "E122.middle", {"position": v(-0.82, 2.82) * mm});
            skLineSegment(sketch, "E123.bottom", {"start": v(0.28, 2.87) * mm, "end": v(0.38, 2.87) * mm});
            skLineSegment(sketch, "E123.top", {"start": v(0.28, 2.77) * mm, "end": v(0.38, 2.77) * mm});
            skLineSegment(sketch, "E123.left", {"start": v(0.28, 2.87) * mm, "end": v(0.28, 2.77) * mm});
            skLineSegment(sketch, "E123.right", {"start": v(0.38, 2.87) * mm, "end": v(0.38, 2.77) * mm});
            skPoint(sketch, "E123.middle", {"position": v(0.33, 2.82) * mm});
            skLineSegment(sketch, "E124.bottom", {"start": v(1.38, 2.84) * mm, "end": v(1.43, 2.84) * mm});
            skLineSegment(sketch, "E124.top", {"start": v(1.38, 2.8) * mm, "end": v(1.43, 2.8) * mm});
            skLineSegment(sketch, "E124.left", {"start": v(1.38, 2.84) * mm, "end": v(1.38, 2.8) * mm});
            skLineSegment(sketch, "E124.right", {"start": v(1.43, 2.84) * mm, "end": v(1.43, 2.8) * mm});
            skPoint(sketch, "E124.middle", {"position": v(1.4, 2.82) * mm});
            skLineSegment(sketch, "E125.bottom", {"start": v(2.43, 2.83) * mm, "end": v(2.46, 2.83) * mm});
            skLineSegment(sketch, "E125.top", {"start": v(2.43, 2.8) * mm, "end": v(2.46, 2.8) * mm});
            skLineSegment(sketch, "E125.left", {"start": v(2.43, 2.83) * mm, "end": v(2.43, 2.8) * mm});
            skLineSegment(sketch, "E125.right", {"start": v(2.46, 2.83) * mm, "end": v(2.46, 2.8) * mm});
            skPoint(sketch, "E125.middle", {"position": v(2.44, 2.82) * mm});
            skLineSegment(sketch, "E126.bottom", {"start": v(3.46, 2.83) * mm, "end": v(3.48, 2.83) * mm});
            skLineSegment(sketch, "E126.top", {"start": v(3.46, 2.8) * mm, "end": v(3.48, 2.8) * mm});
            skLineSegment(sketch, "E126.left", {"start": v(3.46, 2.83) * mm, "end": v(3.46, 2.8) * mm});
            skLineSegment(sketch, "E126.right", {"start": v(3.48, 2.83) * mm, "end": v(3.48, 2.8) * mm});
            skPoint(sketch, "E126.middle", {"position": v(3.47, 2.82) * mm});
            skLineSegment(sketch, "E127.bottom", {"start": v(4.48, 2.83) * mm, "end": v(4.5, 2.83) * mm});
            skLineSegment(sketch, "E127.top", {"start": v(4.48, 2.81) * mm, "end": v(4.5, 2.81) * mm});
            skLineSegment(sketch, "E127.left", {"start": v(4.48, 2.83) * mm, "end": v(4.48, 2.81) * mm});
            skLineSegment(sketch, "E127.right", {"start": v(4.5, 2.83) * mm, "end": v(4.5, 2.81) * mm});
            skPoint(sketch, "E127.middle", {"position": v(4.5, 2.82) * mm});
            skLineSegment(sketch, "E128.bottom", {"start": v(5.5, 2.83) * mm, "end": v(5.52, 2.83) * mm});
            skLineSegment(sketch, "E128.top", {"start": v(5.5, 2.81) * mm, "end": v(5.52, 2.81) * mm});
            skLineSegment(sketch, "E128.left", {"start": v(5.5, 2.83) * mm, "end": v(5.5, 2.81) * mm});
            skLineSegment(sketch, "E128.right", {"start": v(5.52, 2.83) * mm, "end": v(5.52, 2.81) * mm});
            skPoint(sketch, "E128.middle", {"position": v(5.51, 2.82) * mm});
            skLineSegment(sketch, "E129.bottom", {"start": v(-3.72, 3.07) * mm, "end": v(-3.22, 3.07) * mm});
            skLineSegment(sketch, "E129.top", {"start": v(-3.72, 2.57) * mm, "end": v(-3.22, 2.57) * mm});
            skLineSegment(sketch, "E129.left", {"start": v(-3.72, 3.07) * mm, "end": v(-3.72, 2.57) * mm});
            skLineSegment(sketch, "E129.right", {"start": v(-3.22, 3.07) * mm, "end": v(-3.22, 2.57) * mm});
            skPoint(sketch, "E129.middle", {"position": v(-3.47, 2.82) * mm});
            skLineSegment(sketch, "E130.bottom", {"start": v(-2.22, 2.97) * mm, "end": v(-1.92, 2.97) * mm});
            skLineSegment(sketch, "E130.top", {"start": v(-2.22, 2.67) * mm, "end": v(-1.92, 2.67) * mm});
            skLineSegment(sketch, "E130.left", {"start": v(-2.22, 2.97) * mm, "end": v(-2.22, 2.67) * mm});
            skLineSegment(sketch, "E130.right", {"start": v(-1.92, 2.97) * mm, "end": v(-1.92, 2.67) * mm});
            skPoint(sketch, "E130.middle", {"position": v(-2.07, 2.82) * mm});
            skLineSegment(sketch, "E131.bottom", {"start": v(-5.52, 1.42) * mm, "end": v(-4.72, 1.42) * mm});
            skLineSegment(sketch, "E131.top", {"start": v(-5.52, 0.62) * mm, "end": v(-4.72, 0.62) * mm});
            skLineSegment(sketch, "E131.left", {"start": v(-5.52, 1.42) * mm, "end": v(-5.52, 0.62) * mm});
            skLineSegment(sketch, "E131.right", {"start": v(-4.72, 1.42) * mm, "end": v(-4.72, 0.62) * mm});
            skPoint(sketch, "E131.middle", {"position": v(-5.12, 1.02) * mm});
            skLineSegment(sketch, "E132.bottom", {"start": v(-0.92, 1.12) * mm, "end": v(-0.72, 1.12) * mm});
            skLineSegment(sketch, "E132.top", {"start": v(-0.92, 0.92) * mm, "end": v(-0.72, 0.92) * mm});
            skLineSegment(sketch, "E132.left", {"start": v(-0.92, 1.12) * mm, "end": v(-0.92, 0.92) * mm});
            skLineSegment(sketch, "E132.right", {"start": v(-0.72, 1.12) * mm, "end": v(-0.72, 0.92) * mm});
            skPoint(sketch, "E132.middle", {"position": v(-0.82, 1.02) * mm});
            skLineSegment(sketch, "E133.bottom", {"start": v(0.28, 1.07) * mm, "end": v(0.38, 1.07) * mm});
            skLineSegment(sketch, "E133.top", {"start": v(0.28, 0.97) * mm, "end": v(0.38, 0.97) * mm});
            skLineSegment(sketch, "E133.left", {"start": v(0.28, 1.07) * mm, "end": v(0.28, 0.97) * mm});
            skLineSegment(sketch, "E133.right", {"start": v(0.38, 1.07) * mm, "end": v(0.38, 0.97) * mm});
            skPoint(sketch, "E133.middle", {"position": v(0.33, 1.02) * mm});
            skLineSegment(sketch, "E134.bottom", {"start": v(1.38, 1.04) * mm, "end": v(1.43, 1.04) * mm});
            skLineSegment(sketch, "E134.top", {"start": v(1.38, 1) * mm, "end": v(1.43, 1) * mm});
            skLineSegment(sketch, "E134.left", {"start": v(1.38, 1.04) * mm, "end": v(1.38, 1) * mm});
            skLineSegment(sketch, "E134.right", {"start": v(1.43, 1.04) * mm, "end": v(1.43, 1) * mm});
            skPoint(sketch, "E134.middle", {"position": v(1.4, 1.02) * mm});
            skLineSegment(sketch, "E135.bottom", {"start": v(2.43, 1.03) * mm, "end": v(2.46, 1.03) * mm});
            skLineSegment(sketch, "E135.top", {"start": v(2.43, 1) * mm, "end": v(2.46, 1) * mm});
            skLineSegment(sketch, "E135.left", {"start": v(2.43, 1.03) * mm, "end": v(2.43, 1) * mm});
            skLineSegment(sketch, "E135.right", {"start": v(2.46, 1.03) * mm, "end": v(2.46, 1) * mm});
            skPoint(sketch, "E135.middle", {"position": v(2.45, 1.02) * mm});
            skLineSegment(sketch, "E136.bottom", {"start": v(3.46, 1.03) * mm, "end": v(3.48, 1.03) * mm});
            skLineSegment(sketch, "E136.top", {"start": v(3.46, 1) * mm, "end": v(3.48, 1) * mm});
            skLineSegment(sketch, "E136.left", {"start": v(3.46, 1.03) * mm, "end": v(3.46, 1) * mm});
            skLineSegment(sketch, "E136.right", {"start": v(3.48, 1.03) * mm, "end": v(3.48, 1) * mm});
            skPoint(sketch, "E136.middle", {"position": v(3.47, 1.02) * mm});
            skLineSegment(sketch, "E137.bottom", {"start": v(4.48, 1.03) * mm, "end": v(4.5, 1.03) * mm});
            skLineSegment(sketch, "E137.top", {"start": v(4.48, 1) * mm, "end": v(4.5, 1) * mm});
            skLineSegment(sketch, "E137.left", {"start": v(4.48, 1.03) * mm, "end": v(4.48, 1) * mm});
            skLineSegment(sketch, "E137.right", {"start": v(4.5, 1.03) * mm, "end": v(4.5, 1) * mm});
            skPoint(sketch, "E137.middle", {"position": v(4.5, 1.02) * mm});
            skLineSegment(sketch, "E138.bottom", {"start": v(5.5, 1.03) * mm, "end": v(5.52, 1.03) * mm});
            skLineSegment(sketch, "E138.top", {"start": v(5.5, 1.01) * mm, "end": v(5.52, 1.01) * mm});
            skLineSegment(sketch, "E138.left", {"start": v(5.5, 1.03) * mm, "end": v(5.5, 1.01) * mm});
            skLineSegment(sketch, "E138.right", {"start": v(5.52, 1.03) * mm, "end": v(5.52, 1.01) * mm});
            skPoint(sketch, "E138.middle", {"position": v(5.51, 1.02) * mm});
            skLineSegment(sketch, "E139.bottom", {"start": v(-3.72, 1.27) * mm, "end": v(-3.22, 1.27) * mm});
            skLineSegment(sketch, "E139.top", {"start": v(-3.72, 0.77) * mm, "end": v(-3.22, 0.77) * mm});
            skLineSegment(sketch, "E139.left", {"start": v(-3.72, 1.27) * mm, "end": v(-3.72, 0.77) * mm});
            skLineSegment(sketch, "E139.right", {"start": v(-3.22, 1.27) * mm, "end": v(-3.22, 0.77) * mm});
            skPoint(sketch, "E139.middle", {"position": v(-3.47, 1.02) * mm});
            skLineSegment(sketch, "E140.bottom", {"start": v(-2.22, 1.17) * mm, "end": v(-1.92, 1.17) * mm});
            skLineSegment(sketch, "E140.top", {"start": v(-2.22, 0.87) * mm, "end": v(-1.92, 0.87) * mm});
            skLineSegment(sketch, "E140.left", {"start": v(-2.22, 1.17) * mm, "end": v(-2.22, 0.87) * mm});
            skLineSegment(sketch, "E140.right", {"start": v(-1.92, 1.17) * mm, "end": v(-1.92, 0.87) * mm});
            skPoint(sketch, "E140.middle", {"position": v(-2.07, 1.02) * mm});
            skSolve(sketch);
        }
        {
            var Q0;
            Q0=makeQuery(id+"F4.imprint","IMPRINT",FACE,{"disambiguationData":[TD([[makeQuery(id+"F4.imprint","IMPRINT",EDGE,{"derivedFrom":sQuery(id+"F4.wireOp",EDGE,"E51")}),1.0]])]});
            var Q1;
            Q1=makeQuery(id+"F4.imprint","IMPRINT",FACE,{"disambiguationData":[TD([[makeQuery(id+"F4.imprint","IMPRINT",EDGE,{"derivedFrom":sQuery(id+"F4.wireOp",EDGE,"E52")}),1.0]])]});
            var Q2;
            Q2=makeQuery(id+"F4.imprint","IMPRINT",FACE,{"disambiguationData":[TD([[makeQuery(id+"F4.imprint","IMPRINT",EDGE,{"derivedFrom":sQuery(id+"F4.wireOp",EDGE,"E53")}),1.0]])]});
            var Q3;
            Q3=makeQuery(id+"F4.imprint","IMPRINT",FACE,{"disambiguationData":[TD([[makeQuery(id+"F4.imprint","IMPRINT",EDGE,{"derivedFrom":sQuery(id+"F4.wireOp",EDGE,"E54")}),1.0]])]});
            var Q4;
            Q4=makeQuery(id+"F4.imprint","IMPRINT",FACE,{"disambiguationData":[TD([[makeQuery(id+"F4.imprint","IMPRINT",EDGE,{"derivedFrom":sQuery(id+"F4.wireOp",EDGE,"E55")}),1.0]])]});
            var Q5;
            Q5=makeQuery(id+"F4.imprint","IMPRINT",FACE,{"disambiguationData":[TD([[makeQuery(id+"F4.imprint","IMPRINT",EDGE,{"derivedFrom":sQuery(id+"F4.wireOp",EDGE,"E56")}),1.0]])]});
            var Q6;
            Q6=makeQuery(id+"F4.imprint","IMPRINT",FACE,{"disambiguationData":[TD([[makeQuery(id+"F4.imprint","IMPRINT",EDGE,{"derivedFrom":sQuery(id+"F4.wireOp",EDGE,"E57")}),1.0]])]});
            var Q7;
            Q7=makeQuery(id+"F4.imprint","IMPRINT",FACE,{"disambiguationData":[TD([[makeQuery(id+"F4.imprint","IMPRINT",EDGE,{"derivedFrom":sQuery(id+"F4.wireOp",EDGE,"E60")}),1.0]])]});
            var Q8;
            Q8=makeQuery(id+"F4.imprint","IMPRINT",FACE,{"disambiguationData":[TD([[makeQuery(id+"F4.imprint","IMPRINT",EDGE,{"derivedFrom":sQuery(id+"F4.wireOp",EDGE,"E58")}),1.0]])]});
            var Q9;
            Q9=makeQuery(id+"F4.imprint","IMPRINT",FACE,{"disambiguationData":[TD([[makeQuery(id+"F4.imprint","IMPRINT",EDGE,{"derivedFrom":sQuery(id+"F4.wireOp",EDGE,"E59")}),1.0]])]});
            extrude(context, id + "F7", {"entities" : qUnion([Q0, Q1, Q2, Q3, Q4, Q5, Q6, Q7, Q8, Q9]), "operationType" : NewBodyOperationType.ADD, "depth" : .25 * mm, "offsetDistance" : 25 * mm});
        }
        {
            var Q0;
            Q0=makeQuery(id+"F4.imprint","IMPRINT",FACE,{"disambiguationData":[TD([[makeQuery(id+"F4.imprint","IMPRINT",EDGE,{"derivedFrom":sQuery(id+"F4.wireOp",EDGE,"E61")}),1.0]])]});
            var Q1;
            Q1=makeQuery(id+"F4.imprint","IMPRINT",FACE,{"disambiguationData":[TD([[makeQuery(id+"F4.imprint","IMPRINT",EDGE,{"derivedFrom":sQuery(id+"F4.wireOp",EDGE,"E62")}),1.0]])]});
            var Q2;
            Q2=makeQuery(id+"F4.imprint","IMPRINT",FACE,{"disambiguationData":[TD([[makeQuery(id+"F4.imprint","IMPRINT",EDGE,{"derivedFrom":sQuery(id+"F4.wireOp",EDGE,"E63")}),1.0]])]});
            var Q3;
            Q3=makeQuery(id+"F4.imprint","IMPRINT",FACE,{"disambiguationData":[TD([[makeQuery(id+"F4.imprint","IMPRINT",EDGE,{"derivedFrom":sQuery(id+"F4.wireOp",EDGE,"E64")}),1.0]])]});
            var Q4;
            Q4=makeQuery(id+"F4.imprint","IMPRINT",FACE,{"disambiguationData":[TD([[makeQuery(id+"F4.imprint","IMPRINT",EDGE,{"derivedFrom":sQuery(id+"F4.wireOp",EDGE,"E65")}),1.0]])]});
            var Q5;
            Q5=makeQuery(id+"F4.imprint","IMPRINT",FACE,{"disambiguationData":[TD([[makeQuery(id+"F4.imprint","IMPRINT",EDGE,{"derivedFrom":sQuery(id+"F4.wireOp",EDGE,"E66")}),1.0]])]});
            var Q6;
            Q6=makeQuery(id+"F4.imprint","IMPRINT",FACE,{"disambiguationData":[TD([[makeQuery(id+"F4.imprint","IMPRINT",EDGE,{"derivedFrom":sQuery(id+"F4.wireOp",EDGE,"E67")}),1.0]])]});
            var Q7;
            Q7=makeQuery(id+"F4.imprint","IMPRINT",FACE,{"disambiguationData":[TD([[makeQuery(id+"F4.imprint","IMPRINT",EDGE,{"derivedFrom":sQuery(id+"F4.wireOp",EDGE,"E70")}),1.0]])]});
            var Q8;
            Q8=makeQuery(id+"F4.imprint","IMPRINT",FACE,{"disambiguationData":[TD([[makeQuery(id+"F4.imprint","IMPRINT",EDGE,{"derivedFrom":sQuery(id+"F4.wireOp",EDGE,"E68")}),1.0]])]});
            var Q9;
            Q9=makeQuery(id+"F4.imprint","IMPRINT",FACE,{"disambiguationData":[TD([[makeQuery(id+"F4.imprint","IMPRINT",EDGE,{"derivedFrom":sQuery(id+"F4.wireOp",EDGE,"E69")}),1.0]])]});
            extrude(context, id + "F8", {"entities" : qUnion([Q0, Q1, Q2, Q3, Q4, Q5, Q6, Q7, Q8, Q9]), "operationType" : NewBodyOperationType.ADD, "depth" : .5 * mm, "offsetDistance" : 25 * mm});
        }
        {
            var Q0;
            Q0=makeQuery(id+"F4.imprint","IMPRINT",FACE,{"disambiguationData":[TD([[makeQuery(id+"F4.imprint","IMPRINT",EDGE,{"derivedFrom":sQuery(id+"F4.wireOp",EDGE,"E71")}),1.0]])]});
            var Q1;
            Q1=makeQuery(id+"F4.imprint","IMPRINT",FACE,{"disambiguationData":[TD([[makeQuery(id+"F4.imprint","IMPRINT",EDGE,{"derivedFrom":sQuery(id+"F4.wireOp",EDGE,"E72")}),1.0]])]});
            var Q2;
            Q2=makeQuery(id+"F4.imprint","IMPRINT",FACE,{"disambiguationData":[TD([[makeQuery(id+"F4.imprint","IMPRINT",EDGE,{"derivedFrom":sQuery(id+"F4.wireOp",EDGE,"E73")}),1.0]])]});
            var Q3;
            Q3=makeQuery(id+"F4.imprint","IMPRINT",FACE,{"disambiguationData":[TD([[makeQuery(id+"F4.imprint","IMPRINT",EDGE,{"derivedFrom":sQuery(id+"F4.wireOp",EDGE,"E74")}),1.0]])]});
            var Q4;
            Q4=makeQuery(id+"F4.imprint","IMPRINT",FACE,{"disambiguationData":[TD([[makeQuery(id+"F4.imprint","IMPRINT",EDGE,{"derivedFrom":sQuery(id+"F4.wireOp",EDGE,"E75")}),1.0]])]});
            var Q5;
            Q5=makeQuery(id+"F4.imprint","IMPRINT",FACE,{"disambiguationData":[TD([[makeQuery(id+"F4.imprint","IMPRINT",EDGE,{"derivedFrom":sQuery(id+"F4.wireOp",EDGE,"E76")}),1.0]])]});
            var Q6;
            Q6=makeQuery(id+"F4.imprint","IMPRINT",FACE,{"disambiguationData":[TD([[makeQuery(id+"F4.imprint","IMPRINT",EDGE,{"derivedFrom":sQuery(id+"F4.wireOp",EDGE,"E77")}),1.0]])]});
            var Q7;
            Q7=makeQuery(id+"F4.imprint","IMPRINT",FACE,{"disambiguationData":[TD([[makeQuery(id+"F4.imprint","IMPRINT",EDGE,{"derivedFrom":sQuery(id+"F4.wireOp",EDGE,"E80")}),1.0]])]});
            var Q8;
            Q8=makeQuery(id+"F4.imprint","IMPRINT",FACE,{"disambiguationData":[TD([[makeQuery(id+"F4.imprint","IMPRINT",EDGE,{"derivedFrom":sQuery(id+"F4.wireOp",EDGE,"E78")}),1.0]])]});
            var Q9;
            Q9=makeQuery(id+"F4.imprint","IMPRINT",FACE,{"disambiguationData":[TD([[makeQuery(id+"F4.imprint","IMPRINT",EDGE,{"derivedFrom":sQuery(id+"F4.wireOp",EDGE,"E79")}),1.0]])]});
            extrude(context, id + "F9", {"entities" : qUnion([Q0, Q1, Q2, Q3, Q4, Q5, Q6, Q7, Q8, Q9]), "operationType" : NewBodyOperationType.ADD, "depth" : .1 * mm, "offsetDistance" : 25 * mm});
        }
        {
            var Q0;
            Q0=makeQuery(id+"F3.imprint","IMPRINT",FACE,{"disambiguationData":[TD([[makeQuery(id+"F3.imprint","IMPRINT",EDGE,{"derivedFrom":sQuery(id+"F3.wireOp",EDGE,"E41.bottom")}),-1.0]])]});
            var Q1;
            Q1=makeQuery(id+"F3.imprint","IMPRINT",FACE,{"disambiguationData":[TD([[makeQuery(id+"F3.imprint","IMPRINT",EDGE,{"derivedFrom":sQuery(id+"F3.wireOp",EDGE,"E49.bottom")}),-1.0]])]});
            var Q2;
            Q2=makeQuery(id+"F3.imprint","IMPRINT",FACE,{"disambiguationData":[TD([[makeQuery(id+"F3.imprint","IMPRINT",EDGE,{"derivedFrom":sQuery(id+"F3.wireOp",EDGE,"E50.bottom")}),-1.0]])]});
            var Q3;
            Q3=makeQuery(id+"F3.imprint","IMPRINT",FACE,{"disambiguationData":[TD([[makeQuery(id+"F3.imprint","IMPRINT",EDGE,{"derivedFrom":sQuery(id+"F3.wireOp",EDGE,"E42.bottom")}),-1.0]])]});
            var Q4;
            Q4=makeQuery(id+"F3.imprint","IMPRINT",FACE,{"disambiguationData":[TD([[makeQuery(id+"F3.imprint","IMPRINT",EDGE,{"derivedFrom":sQuery(id+"F3.wireOp",EDGE,"E43.bottom")}),-1.0]])]});
            var Q5;
            Q5=makeQuery(id+"F3.imprint","IMPRINT",FACE,{"disambiguationData":[TD([[makeQuery(id+"F3.imprint","IMPRINT",EDGE,{"derivedFrom":sQuery(id+"F3.wireOp",EDGE,"E44.bottom")}),-1.0]])]});
            var Q6;
            Q6=makeQuery(id+"F3.imprint","IMPRINT",FACE,{"disambiguationData":[TD([[makeQuery(id+"F3.imprint","IMPRINT",EDGE,{"derivedFrom":sQuery(id+"F3.wireOp",EDGE,"E45.bottom")}),-1.0]])]});
            var Q7;
            Q7=makeQuery(id+"F3.imprint","IMPRINT",FACE,{"disambiguationData":[TD([[makeQuery(id+"F3.imprint","IMPRINT",EDGE,{"derivedFrom":sQuery(id+"F3.wireOp",EDGE,"E46.bottom")}),-1.0]])]});
            var Q8;
            Q8=makeQuery(id+"F3.imprint","IMPRINT",FACE,{"disambiguationData":[TD([[makeQuery(id+"F3.imprint","IMPRINT",EDGE,{"derivedFrom":sQuery(id+"F3.wireOp",EDGE,"E47.bottom")}),-1.0]])]});
            var Q9;
            Q9=makeQuery(id+"F3.imprint","IMPRINT",FACE,{"disambiguationData":[TD([[makeQuery(id+"F3.imprint","IMPRINT",EDGE,{"derivedFrom":sQuery(id+"F3.wireOp",EDGE,"E48.bottom")}),-1.0]])]});
            extrude(context, id + "F10", {"entities" : qUnion([Q0, Q1, Q2, Q3, Q4, Q5, Q6, Q7, Q8, Q9]), "operationType" : NewBodyOperationType.ADD, "depth" : .25 * mm, "offsetDistance" : 25 * mm});
        }
        {
            var Q0;
            Q0=makeQuery(id+"F3.imprint","IMPRINT",FACE,{"disambiguationData":[TD([[makeQuery(id+"F3.imprint","IMPRINT",EDGE,{"derivedFrom":sQuery(id+"F3.wireOp",EDGE,"E31.bottom")}),-1.0]])]});
            var Q1;
            Q1=makeQuery(id+"F3.imprint","IMPRINT",FACE,{"disambiguationData":[TD([[makeQuery(id+"F3.imprint","IMPRINT",EDGE,{"derivedFrom":sQuery(id+"F3.wireOp",EDGE,"E39.bottom")}),-1.0]])]});
            var Q2;
            Q2=makeQuery(id+"F3.imprint","IMPRINT",FACE,{"disambiguationData":[TD([[makeQuery(id+"F3.imprint","IMPRINT",EDGE,{"derivedFrom":sQuery(id+"F3.wireOp",EDGE,"E40.bottom")}),-1.0]])]});
            var Q3;
            Q3=makeQuery(id+"F3.imprint","IMPRINT",FACE,{"disambiguationData":[TD([[makeQuery(id+"F3.imprint","IMPRINT",EDGE,{"derivedFrom":sQuery(id+"F3.wireOp",EDGE,"E32.bottom")}),-1.0]])]});
            var Q4;
            Q4=makeQuery(id+"F3.imprint","IMPRINT",FACE,{"disambiguationData":[TD([[makeQuery(id+"F3.imprint","IMPRINT",EDGE,{"derivedFrom":sQuery(id+"F3.wireOp",EDGE,"E33.bottom")}),-1.0]])]});
            var Q5;
            Q5=makeQuery(id+"F3.imprint","IMPRINT",FACE,{"disambiguationData":[TD([[makeQuery(id+"F3.imprint","IMPRINT",EDGE,{"derivedFrom":sQuery(id+"F3.wireOp",EDGE,"E34.bottom")}),-1.0]])]});
            var Q6;
            Q6=makeQuery(id+"F3.imprint","IMPRINT",FACE,{"disambiguationData":[TD([[makeQuery(id+"F3.imprint","IMPRINT",EDGE,{"derivedFrom":sQuery(id+"F3.wireOp",EDGE,"E35.bottom")}),-1.0]])]});
            var Q7;
            Q7=makeQuery(id+"F3.imprint","IMPRINT",FACE,{"disambiguationData":[TD([[makeQuery(id+"F3.imprint","IMPRINT",EDGE,{"derivedFrom":sQuery(id+"F3.wireOp",EDGE,"E36.bottom")}),-1.0]])]});
            var Q8;
            Q8=makeQuery(id+"F3.imprint","IMPRINT",FACE,{"disambiguationData":[TD([[makeQuery(id+"F3.imprint","IMPRINT",EDGE,{"derivedFrom":sQuery(id+"F3.wireOp",EDGE,"E37.bottom")}),-1.0]])]});
            var Q9;
            Q9=makeQuery(id+"F3.imprint","IMPRINT",FACE,{"disambiguationData":[TD([[makeQuery(id+"F3.imprint","IMPRINT",EDGE,{"derivedFrom":sQuery(id+"F3.wireOp",EDGE,"E38.bottom")}),-1.0]])]});
            extrude(context, id + "F11", {"entities" : qUnion([Q0, Q1, Q2, Q3, Q4, Q5, Q6, Q7, Q8, Q9]), "operationType" : NewBodyOperationType.ADD, "depth" : .5 * mm, "offsetDistance" : 25 * mm});
        }
        {
            var Q0;
            Q0=makeQuery(id+"F3.imprint","IMPRINT",FACE,{"disambiguationData":[TD([[makeQuery(id+"F3.imprint","IMPRINT",EDGE,{"derivedFrom":sQuery(id+"F3.wireOp",EDGE,"E21.bottom")}),-1.0]])]});
            var Q1;
            Q1=makeQuery(id+"F3.imprint","IMPRINT",FACE,{"disambiguationData":[TD([[makeQuery(id+"F3.imprint","IMPRINT",EDGE,{"derivedFrom":sQuery(id+"F3.wireOp",EDGE,"E29.bottom")}),-1.0]])]});
            var Q2;
            Q2=makeQuery(id+"F3.imprint","IMPRINT",FACE,{"disambiguationData":[TD([[makeQuery(id+"F3.imprint","IMPRINT",EDGE,{"derivedFrom":sQuery(id+"F3.wireOp",EDGE,"E30.bottom")}),-1.0]])]});
            var Q3;
            Q3=makeQuery(id+"F3.imprint","IMPRINT",FACE,{"disambiguationData":[TD([[makeQuery(id+"F3.imprint","IMPRINT",EDGE,{"derivedFrom":sQuery(id+"F3.wireOp",EDGE,"E22.bottom")}),-1.0]])]});
            var Q4;
            Q4=makeQuery(id+"F3.imprint","IMPRINT",FACE,{"disambiguationData":[TD([[makeQuery(id+"F3.imprint","IMPRINT",EDGE,{"derivedFrom":sQuery(id+"F3.wireOp",EDGE,"E23.bottom")}),-1.0]])]});
            var Q5;
            Q5=makeQuery(id+"F3.imprint","IMPRINT",FACE,{"disambiguationData":[TD([[makeQuery(id+"F3.imprint","IMPRINT",EDGE,{"derivedFrom":sQuery(id+"F3.wireOp",EDGE,"E24.bottom")}),-1.0]])]});
            var Q6;
            Q6=makeQuery(id+"F3.imprint","IMPRINT",FACE,{"disambiguationData":[TD([[makeQuery(id+"F3.imprint","IMPRINT",EDGE,{"derivedFrom":sQuery(id+"F3.wireOp",EDGE,"E25.bottom")}),-1.0]])]});
            var Q7;
            Q7=makeQuery(id+"F3.imprint","IMPRINT",FACE,{"disambiguationData":[TD([[makeQuery(id+"F3.imprint","IMPRINT",EDGE,{"derivedFrom":sQuery(id+"F3.wireOp",EDGE,"E26.bottom")}),-1.0]])]});
            var Q8;
            Q8=makeQuery(id+"F3.imprint","IMPRINT",FACE,{"disambiguationData":[TD([[makeQuery(id+"F3.imprint","IMPRINT",EDGE,{"derivedFrom":sQuery(id+"F3.wireOp",EDGE,"E27.bottom")}),-1.0]])]});
            var Q9;
            Q9=makeQuery(id+"F3.imprint","IMPRINT",FACE,{"disambiguationData":[TD([[makeQuery(id+"F3.imprint","IMPRINT",EDGE,{"derivedFrom":sQuery(id+"F3.wireOp",EDGE,"E28.bottom")}),-1.0]])]});
            extrude(context, id + "F12", {"entities" : qUnion([Q0, Q1, Q2, Q3, Q4, Q5, Q6, Q7, Q8, Q9]), "operationType" : NewBodyOperationType.ADD, "depth" : .1 * mm, "offsetDistance" : 25 * mm});
        }
        {
            var Q0;
            Q0=makeQuery(id+"F6.imprint","IMPRINT",FACE,{"disambiguationData":[TD([[makeQuery(id+"F6.imprint","IMPRINT",EDGE,{"derivedFrom":sQuery(id+"F6.wireOp",EDGE,"E101")}),1.0]])]});
            var Q1;
            Q1=makeQuery(id+"F6.imprint","IMPRINT",FACE,{"disambiguationData":[TD([[makeQuery(id+"F6.imprint","IMPRINT",EDGE,{"derivedFrom":sQuery(id+"F6.wireOp",EDGE,"E102")}),1.0]])]});
            var Q2;
            Q2=makeQuery(id+"F6.imprint","IMPRINT",FACE,{"disambiguationData":[TD([[makeQuery(id+"F6.imprint","IMPRINT",EDGE,{"derivedFrom":sQuery(id+"F6.wireOp",EDGE,"E103")}),1.0]])]});
            var Q3;
            Q3=makeQuery(id+"F6.imprint","IMPRINT",FACE,{"disambiguationData":[TD([[makeQuery(id+"F6.imprint","IMPRINT",EDGE,{"derivedFrom":sQuery(id+"F6.wireOp",EDGE,"E104")}),1.0]])]});
            var Q4;
            Q4=makeQuery(id+"F6.imprint","IMPRINT",FACE,{"disambiguationData":[TD([[makeQuery(id+"F6.imprint","IMPRINT",EDGE,{"derivedFrom":sQuery(id+"F6.wireOp",EDGE,"E105")}),1.0]])]});
            var Q5;
            Q5=makeQuery(id+"F6.imprint","IMPRINT",FACE,{"disambiguationData":[TD([[makeQuery(id+"F6.imprint","IMPRINT",EDGE,{"derivedFrom":sQuery(id+"F6.wireOp",EDGE,"E106")}),1.0]])]});
            var Q6;
            Q6=makeQuery(id+"F6.imprint","IMPRINT",FACE,{"disambiguationData":[TD([[makeQuery(id+"F6.imprint","IMPRINT",EDGE,{"derivedFrom":sQuery(id+"F6.wireOp",EDGE,"E107")}),1.0]])]});
            var Q7;
            Q7=makeQuery(id+"F6.imprint","IMPRINT",FACE,{"disambiguationData":[TD([[makeQuery(id+"F6.imprint","IMPRINT",EDGE,{"derivedFrom":sQuery(id+"F6.wireOp",EDGE,"E110")}),1.0]])]});
            var Q8;
            Q8=makeQuery(id+"F6.imprint","IMPRINT",FACE,{"disambiguationData":[TD([[makeQuery(id+"F6.imprint","IMPRINT",EDGE,{"derivedFrom":sQuery(id+"F6.wireOp",EDGE,"E108")}),1.0]])]});
            var Q9;
            Q9=makeQuery(id+"F6.imprint","IMPRINT",FACE,{"disambiguationData":[TD([[makeQuery(id+"F6.imprint","IMPRINT",EDGE,{"derivedFrom":sQuery(id+"F6.wireOp",EDGE,"E109")}),1.0]])]});
            var Q10;
            Q10=makeQuery(id+"F6.imprint","IMPRINT",FACE,{"disambiguationData":[TD([[makeQuery(id+"F6.imprint","IMPRINT",EDGE,{"derivedFrom":sQuery(id+"F6.wireOp",EDGE,"E111.bottom")}),-1.0]])]});
            var Q11;
            Q11=makeQuery(id+"F6.imprint","IMPRINT",FACE,{"disambiguationData":[TD([[makeQuery(id+"F6.imprint","IMPRINT",EDGE,{"derivedFrom":sQuery(id+"F6.wireOp",EDGE,"E119.bottom")}),-1.0]])]});
            var Q12;
            Q12=makeQuery(id+"F6.imprint","IMPRINT",FACE,{"disambiguationData":[TD([[makeQuery(id+"F6.imprint","IMPRINT",EDGE,{"derivedFrom":sQuery(id+"F6.wireOp",EDGE,"E120.bottom")}),-1.0]])]});
            var Q13;
            Q13=makeQuery(id+"F6.imprint","IMPRINT",FACE,{"disambiguationData":[TD([[makeQuery(id+"F6.imprint","IMPRINT",EDGE,{"derivedFrom":sQuery(id+"F6.wireOp",EDGE,"E112.bottom")}),-1.0]])]});
            var Q14;
            Q14=makeQuery(id+"F6.imprint","IMPRINT",FACE,{"disambiguationData":[TD([[makeQuery(id+"F6.imprint","IMPRINT",EDGE,{"derivedFrom":sQuery(id+"F6.wireOp",EDGE,"E113.bottom")}),-1.0]])]});
            var Q15;
            Q15=makeQuery(id+"F6.imprint","IMPRINT",FACE,{"disambiguationData":[TD([[makeQuery(id+"F6.imprint","IMPRINT",EDGE,{"derivedFrom":sQuery(id+"F6.wireOp",EDGE,"E114.bottom")}),-1.0]])]});
            var Q16;
            Q16=makeQuery(id+"F6.imprint","IMPRINT",FACE,{"disambiguationData":[TD([[makeQuery(id+"F6.imprint","IMPRINT",EDGE,{"derivedFrom":sQuery(id+"F6.wireOp",EDGE,"E115.bottom")}),-1.0]])]});
            var Q17;
            Q17=makeQuery(id+"F6.imprint","IMPRINT",FACE,{"disambiguationData":[TD([[makeQuery(id+"F6.imprint","IMPRINT",EDGE,{"derivedFrom":sQuery(id+"F6.wireOp",EDGE,"E116.bottom")}),-1.0]])]});
            var Q18;
            Q18=makeQuery(id+"F6.imprint","IMPRINT",FACE,{"disambiguationData":[TD([[makeQuery(id+"F6.imprint","IMPRINT",EDGE,{"derivedFrom":sQuery(id+"F6.wireOp",EDGE,"E117.bottom")}),-1.0]])]});
            var Q19;
            Q19=makeQuery(id+"F6.imprint","IMPRINT",FACE,{"disambiguationData":[TD([[makeQuery(id+"F6.imprint","IMPRINT",EDGE,{"derivedFrom":sQuery(id+"F6.wireOp",EDGE,"E118.bottom")}),-1.0]])]});
            extrude(context, id + "F13", {"entities" : qUnion([Q0, Q1, Q2, Q3, Q4, Q5, Q6, Q7, Q8, Q9, Q10, Q11, Q12, Q13, Q14, Q15, Q16, Q17, Q18, Q19]), "operationType" : NewBodyOperationType.REMOVE, "oppositeDirection" : true, "depth" : .1 * mm, "offsetDistance" : 25 * mm});
        }
        {
            var Q0;
            Q0=makeQuery(id+"F6.imprint","IMPRINT",FACE,{"disambiguationData":[TD([[makeQuery(id+"F6.imprint","IMPRINT",EDGE,{"derivedFrom":sQuery(id+"F6.wireOp",EDGE,"E121.bottom")}),-1.0]])]});
            var Q1;
            Q1=makeQuery(id+"F6.imprint","IMPRINT",FACE,{"disambiguationData":[TD([[makeQuery(id+"F6.imprint","IMPRINT",EDGE,{"derivedFrom":sQuery(id+"F6.wireOp",EDGE,"E129.bottom")}),-1.0]])]});
            var Q2;
            Q2=makeQuery(id+"F6.imprint","IMPRINT",FACE,{"disambiguationData":[TD([[makeQuery(id+"F6.imprint","IMPRINT",EDGE,{"derivedFrom":sQuery(id+"F6.wireOp",EDGE,"E130.bottom")}),-1.0]])]});
            var Q3;
            Q3=makeQuery(id+"F6.imprint","IMPRINT",FACE,{"disambiguationData":[TD([[makeQuery(id+"F6.imprint","IMPRINT",EDGE,{"derivedFrom":sQuery(id+"F6.wireOp",EDGE,"E122.bottom")}),-1.0]])]});
            var Q4;
            Q4=makeQuery(id+"F6.imprint","IMPRINT",FACE,{"disambiguationData":[TD([[makeQuery(id+"F6.imprint","IMPRINT",EDGE,{"derivedFrom":sQuery(id+"F6.wireOp",EDGE,"E123.bottom")}),-1.0]])]});
            var Q5;
            Q5=makeQuery(id+"F6.imprint","IMPRINT",FACE,{"disambiguationData":[TD([[makeQuery(id+"F6.imprint","IMPRINT",EDGE,{"derivedFrom":sQuery(id+"F6.wireOp",EDGE,"E124.bottom")}),-1.0]])]});
            var Q6;
            Q6=makeQuery(id+"F6.imprint","IMPRINT",FACE,{"disambiguationData":[TD([[makeQuery(id+"F6.imprint","IMPRINT",EDGE,{"derivedFrom":sQuery(id+"F6.wireOp",EDGE,"E125.bottom")}),-1.0]])]});
            var Q7;
            Q7=makeQuery(id+"F6.imprint","IMPRINT",FACE,{"disambiguationData":[TD([[makeQuery(id+"F6.imprint","IMPRINT",EDGE,{"derivedFrom":sQuery(id+"F6.wireOp",EDGE,"E126.bottom")}),-1.0]])]});
            var Q8;
            Q8=makeQuery(id+"F6.imprint","IMPRINT",FACE,{"disambiguationData":[TD([[makeQuery(id+"F6.imprint","IMPRINT",EDGE,{"derivedFrom":sQuery(id+"F6.wireOp",EDGE,"E127.bottom")}),-1.0]])]});
            var Q9;
            Q9=makeQuery(id+"F6.imprint","IMPRINT",FACE,{"disambiguationData":[TD([[makeQuery(id+"F6.imprint","IMPRINT",EDGE,{"derivedFrom":sQuery(id+"F6.wireOp",EDGE,"E128.bottom")}),-1.0]])]});
            var Q10;
            Q10=makeQuery(id+"F6.imprint","IMPRINT",FACE,{"disambiguationData":[TD([[makeQuery(id+"F6.imprint","IMPRINT",EDGE,{"derivedFrom":sQuery(id+"F6.wireOp",EDGE,"E91")}),1.0]])]});
            var Q11;
            Q11=makeQuery(id+"F6.imprint","IMPRINT",FACE,{"disambiguationData":[TD([[makeQuery(id+"F6.imprint","IMPRINT",EDGE,{"derivedFrom":sQuery(id+"F6.wireOp",EDGE,"E92")}),1.0]])]});
            var Q12;
            Q12=makeQuery(id+"F6.imprint","IMPRINT",FACE,{"disambiguationData":[TD([[makeQuery(id+"F6.imprint","IMPRINT",EDGE,{"derivedFrom":sQuery(id+"F6.wireOp",EDGE,"E93")}),1.0]])]});
            var Q13;
            Q13=makeQuery(id+"F6.imprint","IMPRINT",FACE,{"disambiguationData":[TD([[makeQuery(id+"F6.imprint","IMPRINT",EDGE,{"derivedFrom":sQuery(id+"F6.wireOp",EDGE,"E94")}),1.0]])]});
            var Q14;
            Q14=makeQuery(id+"F6.imprint","IMPRINT",FACE,{"disambiguationData":[TD([[makeQuery(id+"F6.imprint","IMPRINT",EDGE,{"derivedFrom":sQuery(id+"F6.wireOp",EDGE,"E95")}),1.0]])]});
            var Q15;
            Q15=makeQuery(id+"F6.imprint","IMPRINT",FACE,{"disambiguationData":[TD([[makeQuery(id+"F6.imprint","IMPRINT",EDGE,{"derivedFrom":sQuery(id+"F6.wireOp",EDGE,"E96")}),1.0]])]});
            var Q16;
            Q16=makeQuery(id+"F6.imprint","IMPRINT",FACE,{"disambiguationData":[TD([[makeQuery(id+"F6.imprint","IMPRINT",EDGE,{"derivedFrom":sQuery(id+"F6.wireOp",EDGE,"E97")}),1.0]])]});
            var Q17;
            Q17=makeQuery(id+"F6.imprint","IMPRINT",FACE,{"disambiguationData":[TD([[makeQuery(id+"F6.imprint","IMPRINT",EDGE,{"derivedFrom":sQuery(id+"F6.wireOp",EDGE,"E100")}),1.0]])]});
            var Q18;
            Q18=makeQuery(id+"F6.imprint","IMPRINT",FACE,{"disambiguationData":[TD([[makeQuery(id+"F6.imprint","IMPRINT",EDGE,{"derivedFrom":sQuery(id+"F6.wireOp",EDGE,"E98")}),1.0]])]});
            var Q19;
            Q19=makeQuery(id+"F6.imprint","IMPRINT",FACE,{"disambiguationData":[TD([[makeQuery(id+"F6.imprint","IMPRINT",EDGE,{"derivedFrom":sQuery(id+"F6.wireOp",EDGE,"E99")}),1.0]])]});
            extrude(context, id + "F14", {"entities" : qUnion([Q0, Q1, Q2, Q3, Q4, Q5, Q6, Q7, Q8, Q9, Q10, Q11, Q12, Q13, Q14, Q15, Q16, Q17, Q18, Q19]), "operationType" : NewBodyOperationType.REMOVE, "oppositeDirection" : true, "depth" : .5 * mm, "offsetDistance" : 25 * mm});
        }
        {
            var Q0;
            Q0=makeQuery(id+"F6.imprint","IMPRINT",FACE,{"disambiguationData":[TD([[makeQuery(id+"F6.imprint","IMPRINT",EDGE,{"derivedFrom":sQuery(id+"F6.wireOp",EDGE,"E131.bottom")}),-1.0]])]});
            var Q1;
            Q1=makeQuery(id+"F6.imprint","IMPRINT",FACE,{"disambiguationData":[TD([[makeQuery(id+"F6.imprint","IMPRINT",EDGE,{"derivedFrom":sQuery(id+"F6.wireOp",EDGE,"E139.bottom")}),-1.0]])]});
            var Q2;
            Q2=makeQuery(id+"F6.imprint","IMPRINT",FACE,{"disambiguationData":[TD([[makeQuery(id+"F6.imprint","IMPRINT",EDGE,{"derivedFrom":sQuery(id+"F6.wireOp",EDGE,"E140.bottom")}),-1.0]])]});
            var Q3;
            Q3=makeQuery(id+"F6.imprint","IMPRINT",FACE,{"disambiguationData":[TD([[makeQuery(id+"F6.imprint","IMPRINT",EDGE,{"derivedFrom":sQuery(id+"F6.wireOp",EDGE,"E132.bottom")}),-1.0]])]});
            var Q4;
            Q4=makeQuery(id+"F6.imprint","IMPRINT",FACE,{"disambiguationData":[TD([[makeQuery(id+"F6.imprint","IMPRINT",EDGE,{"derivedFrom":sQuery(id+"F6.wireOp",EDGE,"E133.bottom")}),-1.0]])]});
            var Q5;
            Q5=makeQuery(id+"F6.imprint","IMPRINT",FACE,{"disambiguationData":[TD([[makeQuery(id+"F6.imprint","IMPRINT",EDGE,{"derivedFrom":sQuery(id+"F6.wireOp",EDGE,"E134.bottom")}),-1.0]])]});
            var Q6;
            Q6=makeQuery(id+"F6.imprint","IMPRINT",FACE,{"disambiguationData":[TD([[makeQuery(id+"F6.imprint","IMPRINT",EDGE,{"derivedFrom":sQuery(id+"F6.wireOp",EDGE,"E135.bottom")}),-1.0]])]});
            var Q7;
            Q7=makeQuery(id+"F6.imprint","IMPRINT",FACE,{"disambiguationData":[TD([[makeQuery(id+"F6.imprint","IMPRINT",EDGE,{"derivedFrom":sQuery(id+"F6.wireOp",EDGE,"E136.bottom")}),-1.0]])]});
            var Q8;
            Q8=makeQuery(id+"F6.imprint","IMPRINT",FACE,{"disambiguationData":[TD([[makeQuery(id+"F6.imprint","IMPRINT",EDGE,{"derivedFrom":sQuery(id+"F6.wireOp",EDGE,"E137.bottom")}),-1.0]])]});
            var Q9;
            Q9=makeQuery(id+"F6.imprint","IMPRINT",FACE,{"disambiguationData":[TD([[makeQuery(id+"F6.imprint","IMPRINT",EDGE,{"derivedFrom":sQuery(id+"F6.wireOp",EDGE,"E138.bottom")}),-1.0]])]});
            var Q10;
            Q10=makeQuery(id+"F6.imprint","IMPRINT",FACE,{"disambiguationData":[TD([[makeQuery(id+"F6.imprint","IMPRINT",EDGE,{"derivedFrom":sQuery(id+"F6.wireOp",EDGE,"E81")}),1.0]])]});
            var Q11;
            Q11=makeQuery(id+"F6.imprint","IMPRINT",FACE,{"disambiguationData":[TD([[makeQuery(id+"F6.imprint","IMPRINT",EDGE,{"derivedFrom":sQuery(id+"F6.wireOp",EDGE,"E82")}),1.0]])]});
            var Q12;
            Q12=makeQuery(id+"F6.imprint","IMPRINT",FACE,{"disambiguationData":[TD([[makeQuery(id+"F6.imprint","IMPRINT",EDGE,{"derivedFrom":sQuery(id+"F6.wireOp",EDGE,"E83")}),1.0]])]});
            var Q13;
            Q13=makeQuery(id+"F6.imprint","IMPRINT",FACE,{"disambiguationData":[TD([[makeQuery(id+"F6.imprint","IMPRINT",EDGE,{"derivedFrom":sQuery(id+"F6.wireOp",EDGE,"E84")}),1.0]])]});
            var Q14;
            Q14=makeQuery(id+"F6.imprint","IMPRINT",FACE,{"disambiguationData":[TD([[makeQuery(id+"F6.imprint","IMPRINT",EDGE,{"derivedFrom":sQuery(id+"F6.wireOp",EDGE,"E85")}),1.0]])]});
            var Q15;
            Q15=makeQuery(id+"F6.imprint","IMPRINT",FACE,{"disambiguationData":[TD([[makeQuery(id+"F6.imprint","IMPRINT",EDGE,{"derivedFrom":sQuery(id+"F6.wireOp",EDGE,"E86")}),1.0]])]});
            var Q16;
            Q16=makeQuery(id+"F6.imprint","IMPRINT",FACE,{"disambiguationData":[TD([[makeQuery(id+"F6.imprint","IMPRINT",EDGE,{"derivedFrom":sQuery(id+"F6.wireOp",EDGE,"E87")}),1.0]])]});
            var Q17;
            Q17=makeQuery(id+"F6.imprint","IMPRINT",FACE,{"disambiguationData":[TD([[makeQuery(id+"F6.imprint","IMPRINT",EDGE,{"derivedFrom":sQuery(id+"F6.wireOp",EDGE,"E90")}),1.0]])]});
            var Q18;
            Q18=makeQuery(id+"F6.imprint","IMPRINT",FACE,{"disambiguationData":[TD([[makeQuery(id+"F6.imprint","IMPRINT",EDGE,{"derivedFrom":sQuery(id+"F6.wireOp",EDGE,"E88")}),1.0]])]});
            var Q19;
            Q19=makeQuery(id+"F6.imprint","IMPRINT",FACE,{"disambiguationData":[TD([[makeQuery(id+"F6.imprint","IMPRINT",EDGE,{"derivedFrom":sQuery(id+"F6.wireOp",EDGE,"E89")}),1.0]])]});
            extrude(context, id + "F15", {"entities" : qUnion([Q0, Q1, Q2, Q3, Q4, Q5, Q6, Q7, Q8, Q9, Q10, Q11, Q12, Q13, Q14, Q15, Q16, Q17, Q18, Q19]), "operationType" : NewBodyOperationType.REMOVE, "oppositeDirection" : true, "depth" : .25 * mm, "offsetDistance" : 25 * mm});
        }
    });
